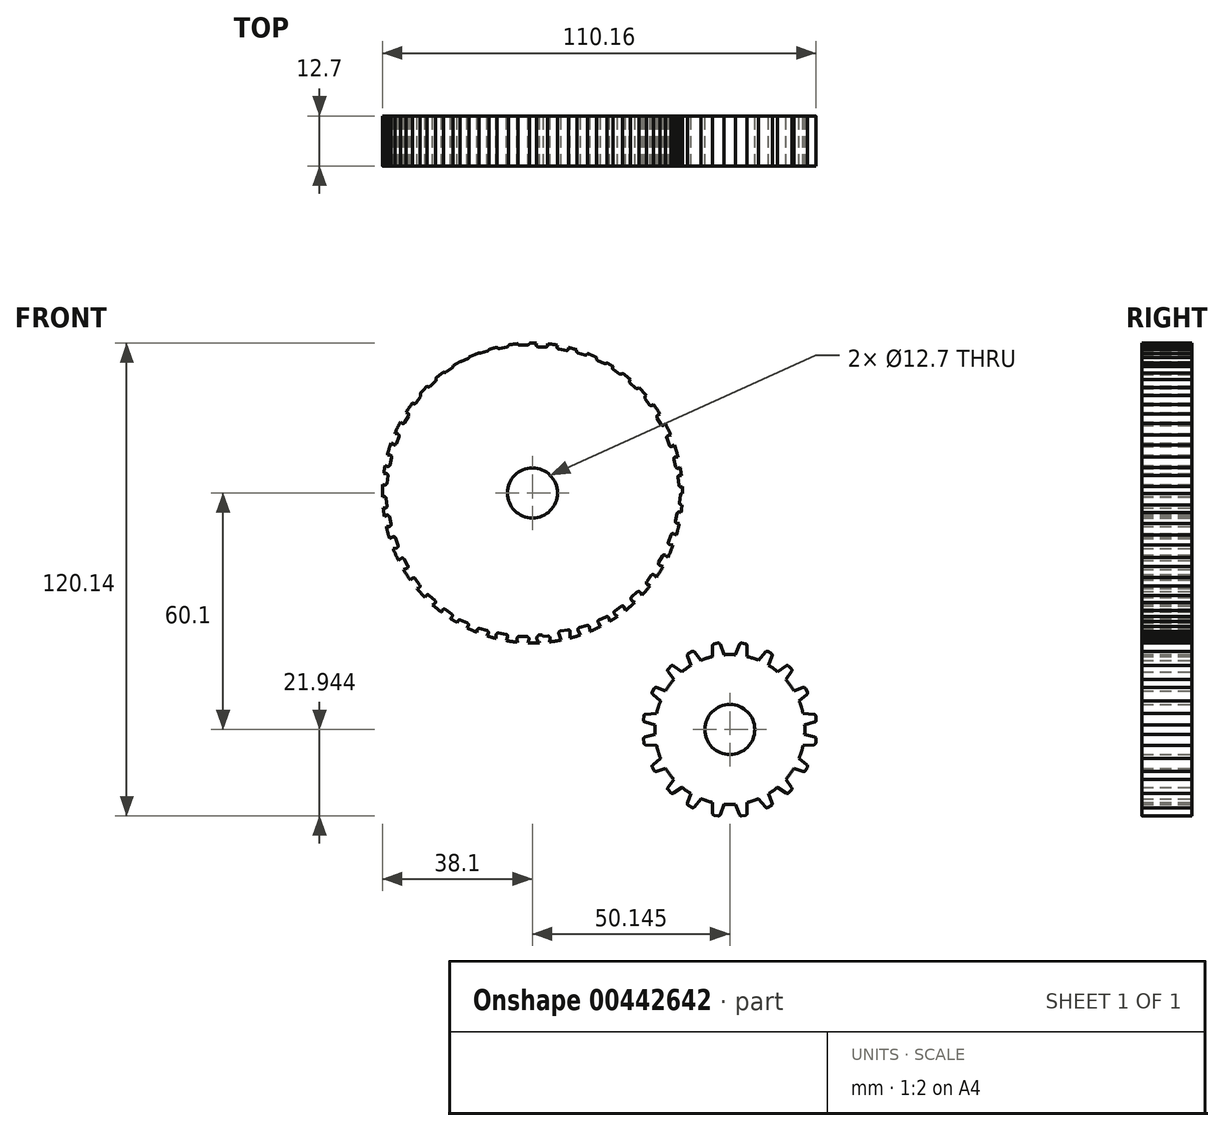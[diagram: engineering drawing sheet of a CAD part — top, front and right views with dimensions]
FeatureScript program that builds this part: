
annotation { "Feature Type Name" : "Feature", "Feature Type Description" : "" }
export const myFeature = defineFeature(function(context is Context, id is Id, definition is map)
    precondition{}
    {
        {
            var Q0;
            Q0=qCreatedBy(makeId("Front.planeOp"),FACE);
            var sketch = newSketch(context, id + "F0", { "sketchPlane" : qUnion([Q0])});
            skCircle(sketch, "E0", {"center": v(-27.1, 27.65) * mm, "radius": 38.1 * mm});
            skCircle(sketch, "E1", {"center": v(-27.1, 27.65) * mm, "radius": 6.35 * mm});
            skLineSegment(sketch, "E2", {"start": v(-65.2, 27.65) * mm, "end": v(11, 27.65) * mm, "construction": true});
            skLineSegment(sketch, "E3", {"start": v(-27.1, 65.75) * mm, "end": v(-27.1, -10.45) * mm, "construction": true});
            skLineSegment(sketch, "E4.MirrorCS", {"start": v(11, 27.65) * mm, "end": v(-65.2, 27.65) * mm, "construction": true});
            skLineSegment(sketch, "E5.MirrorCS", {"start": v(-30.36, 68.9) * mm, "end": v(-28.52, 68.98) * mm, "construction": true});
            skArc(sketch, "E6.MirrorCS", {"start": v(-41.25, 66.38) * mm, "mid": v(-41.16, 66.72) * mm, "end": v(-40.88, 66.92) * mm});
            skArc(sketch, "E7.MirrorCS", {"start": v(-28.95, 68.96) * mm, "mid": v(-28.62, 68.86) * mm, "end": v(-28.43, 68.56) * mm});
            skLineSegment(sketch, "E8.MirrorCS", {"start": v(-28.95, 68.96) * mm, "end": v(-29.93, 68.92) * mm});
            skLineSegment(sketch, "E9.MirrorCS", {"start": v(-39.93, 67.2) * mm, "end": v(-40.88, 66.92) * mm});
            skLineSegment(sketch, "E10.MirrorCS", {"start": v(-36.12, 68.01) * mm, "end": v(-34.3, 68.34) * mm, "construction": true});
            skLineSegment(sketch, "E11.MirrorCS", {"start": v(-55.6, 57.53) * mm, "end": v(-54.24, 58.77) * mm, "construction": true});
            skLineSegment(sketch, "E12.MirrorCS", {"start": v(-66.59, 37.04) * mm, "end": v(-66.8, 36.08) * mm});
            skLineSegment(sketch, "E13.MirrorCS", {"start": v(-64.7, 42.84) * mm, "end": v(-65.03, 41.91) * mm});
            skLineSegment(sketch, "E14.MirrorCS", {"start": v(-45.34, 65.04) * mm, "end": v(-46.25, 64.66) * mm});
            skArc(sketch, "E15.MirrorCS", {"start": v(-54.55, 58.48) * mm, "mid": v(-54.23, 58.61) * mm, "end": v(-53.9, 58.5) * mm});
            skArc(sketch, "E16.MirrorCS", {"start": v(-45.34, 65.04) * mm, "mid": v(-45, 65.06) * mm, "end": v(-44.72, 64.85) * mm});
            skArc(sketch, "E17.MirrorCS", {"start": v(-30.42, 68.48) * mm, "mid": v(-30.25, 68.79) * mm, "end": v(-29.93, 68.92) * mm});
            skLineSegment(sketch, "E18.MirrorCS", {"start": v(-54.55, 58.48) * mm, "end": v(-55.28, 57.82) * mm});
            skLineSegment(sketch, "E19.MirrorCS", {"start": v(-41.3, 66.8) * mm, "end": v(-39.52, 67.3) * mm, "construction": true});
            skArc(sketch, "E20.MirrorCS", {"start": v(-50.97, 61.04) * mm, "mid": v(-51, 61.4) * mm, "end": v(-50.8, 61.68) * mm});
            skArc(sketch, "E21.MirrorCS", {"start": v(-47.4, 60.28) * mm, "mid": v(-47.25, 59.87) * mm, "end": v(-47.46, 59.5) * mm});
            skArc(sketch, "E22.MirrorCS", {"start": v(-39.93, 67.2) * mm, "mid": v(-39.59, 67.17) * mm, "end": v(-39.34, 66.92) * mm});
            skLineSegment(sketch, "E23.MirrorCS", {"start": v(-49.35, 62.2) * mm, "end": v(-47.4, 60.28) * mm});
            skArc(sketch, "E24.MirrorCS", {"start": v(-50, 62.25) * mm, "mid": v(-49.67, 62.34) * mm, "end": v(-49.35, 62.2) * mm});
            skArc(sketch, "E25.MirrorCS", {"start": v(-55.76, 52.86) * mm, "mid": v(-55.48, 52.53) * mm, "end": v(-55.56, 52.1) * mm});
            skLineSegment(sketch, "E26.MirrorCS", {"start": v(-50, 62.25) * mm, "end": v(-50.8, 61.68) * mm});
            skLineSegment(sketch, "E27.MirrorCS", {"start": v(-66.9, 35.66) * mm, "end": v(-66.5, 37.45) * mm, "construction": true});
            skArc(sketch, "E28.MirrorCS", {"start": v(-66.5, 35.5) * mm, "mid": v(-66.76, 35.73) * mm, "end": v(-66.8, 36.08) * mm});
            skArc(sketch, "E29.MirrorCS", {"start": v(-36.12, 67.59) * mm, "mid": v(-36, 67.91) * mm, "end": v(-35.7, 68.09) * mm});
            skLineSegment(sketch, "E30.MirrorCS", {"start": v(-46.65, 64.5) * mm, "end": v(-44.95, 65.2) * mm, "construction": true});
            skArc(sketch, "E31.MirrorCS", {"start": v(-35.51, 64.35) * mm, "mid": v(-35.93, 64.46) * mm, "end": v(-36.1, 64.84) * mm});
            skArc(sketch, "E32.MirrorCS", {"start": v(-46.55, 64.08) * mm, "mid": v(-46.5, 64.42) * mm, "end": v(-46.25, 64.66) * mm});
            skArc(sketch, "E33.MirrorCS", {"start": v(-66.59, 37.04) * mm, "mid": v(-66.4, 37.33) * mm, "end": v(-66.07, 37.43) * mm});
            skArc(sketch, "E34.MirrorCS", {"start": v(-55.37, 57.17) * mm, "mid": v(-55.45, 57.5) * mm, "end": v(-55.28, 57.82) * mm});
            skArc(sketch, "E35.MirrorCS", {"start": v(-34.73, 68.26) * mm, "mid": v(-34.38, 68.2) * mm, "end": v(-34.16, 67.94) * mm});
            skLineSegment(sketch, "E36.MirrorCS", {"start": v(-34.73, 68.26) * mm, "end": v(-35.7, 68.09) * mm});
            skArc(sketch, "E37.MirrorCS", {"start": v(-61.43, 42.72) * mm, "mid": v(-61.08, 42.47) * mm, "end": v(-61.04, 42.05) * mm});
            skArc(sketch, "E38.MirrorCS", {"start": v(-64.7, 42.84) * mm, "mid": v(-64.48, 43.1) * mm, "end": v(-64.14, 43.17) * mm});
            skArc(sketch, "E39.MirrorCS", {"start": v(-67.36, 30.53) * mm, "mid": v(-67.64, 30.74) * mm, "end": v(-67.71, 31.08) * mm});
            skLineSegment(sketch, "E40.MirrorCS", {"start": v(-55.56, 52.1) * mm, "end": v(-56.68, 50.52) * mm});
            skArc(sketch, "E41.MirrorCS", {"start": v(-67.58, 32.05) * mm, "mid": v(-67.42, 32.36) * mm, "end": v(-67.1, 32.5) * mm});
            skLineSegment(sketch, "E42.MirrorCS", {"start": v(-62.75, 47.45) * mm, "end": v(-61.83, 49.04) * mm, "construction": true});
            skArc(sketch, "E43.MirrorCS", {"start": v(-43.23, 62.55) * mm, "mid": v(-43.17, 62.12) * mm, "end": v(-43.46, 61.8) * mm});
            skArc(sketch, "E44.MirrorCS", {"start": v(-59.55, 45.55) * mm, "mid": v(-59.9, 45.3) * mm, "end": v(-60.32, 45.41) * mm});
            skLineSegment(sketch, "E45.MirrorCS", {"start": v(-67.58, 32.05) * mm, "end": v(-67.71, 31.08) * mm});
            skArc(sketch, "E46.MirrorCS", {"start": v(-62.42, 47.17) * mm, "mid": v(-62.6, 47.48) * mm, "end": v(-62.53, 47.82) * mm});
            skLineSegment(sketch, "E47.MirrorCS", {"start": v(-33.6, 64.69) * mm, "end": v(-35.51, 64.35) * mm});
            skArc(sketch, "E48.MirrorCS", {"start": v(-58.85, 47.96) * mm, "mid": v(-58.55, 47.65) * mm, "end": v(-58.58, 47.23) * mm});
            skLineSegment(sketch, "E49.MirrorCS", {"start": v(-67.77, 30.65) * mm, "end": v(-67.53, 32.48) * mm, "construction": true});
            skArc(sketch, "E50.MirrorCS", {"start": v(-30.25, 65.19) * mm, "mid": v(-30.65, 65.35) * mm, "end": v(-30.78, 65.76) * mm});
            skArc(sketch, "E51.MirrorCS", {"start": v(-62.04, 48.67) * mm, "mid": v(-61.77, 48.9) * mm, "end": v(-61.43, 48.9) * mm});
            skLineSegment(sketch, "E52.MirrorCS", {"start": v(-44.72, 64.85) * mm, "end": v(-43.23, 62.55) * mm});
            skArc(sketch, "E53.MirrorCS", {"start": v(-27.84, 65.89) * mm, "mid": v(-27.93, 65.47) * mm, "end": v(-28.32, 65.27) * mm});
            skLineSegment(sketch, "E54.MirrorCS", {"start": v(-62.04, 48.67) * mm, "end": v(-62.53, 47.82) * mm});
            skLineSegment(sketch, "E55.MirrorCS", {"start": v(-53.9, 58.5) * mm, "end": v(-51.73, 56.83) * mm});
            skLineSegment(sketch, "E56.MirrorCS", {"start": v(-43.46, 61.8) * mm, "end": v(-45.25, 61.05) * mm});
            skArc(sketch, "E57.MirrorCS", {"start": v(-40.33, 63.22) * mm, "mid": v(-40.75, 63.29) * mm, "end": v(-40.97, 63.65) * mm});
            skLineSegment(sketch, "E58.MirrorCS", {"start": v(-60.32, 45.41) * mm, "end": v(-62.42, 47.17) * mm});
            skLineSegment(sketch, "E59.MirrorCS", {"start": v(-51.7, 56.05) * mm, "end": v(-53.13, 54.75) * mm});
            skArc(sketch, "E60.MirrorCS", {"start": v(-38.14, 64.46) * mm, "mid": v(-38.14, 64.03) * mm, "end": v(-38.46, 63.75) * mm});
            skLineSegment(sketch, "E61.MirrorCS", {"start": v(-59.68, 52.71) * mm, "end": v(-58.62, 54.21) * mm, "construction": true});
            skArc(sketch, "E62.MirrorCS", {"start": v(-49.04, 58.38) * mm, "mid": v(-49.46, 58.3) * mm, "end": v(-49.8, 58.57) * mm});
            skArc(sketch, "E63.MirrorCS", {"start": v(-61.69, 40.22) * mm, "mid": v(-61.99, 39.91) * mm, "end": v(-62.42, 39.95) * mm});
            skArc(sketch, "E64.MirrorCS", {"start": v(-59.38, 52.41) * mm, "mid": v(-59.53, 52.73) * mm, "end": v(-59.44, 53.06) * mm});
            skLineSegment(sketch, "E65.MirrorCS", {"start": v(-58.58, 47.23) * mm, "end": v(-59.55, 45.55) * mm});
            skArc(sketch, "E66.MirrorCS", {"start": v(-56.68, 50.52) * mm, "mid": v(-57.05, 50.31) * mm, "end": v(-57.46, 50.46) * mm});
            skLineSegment(sketch, "E67.MirrorCS", {"start": v(-65.17, 41.5) * mm, "end": v(-64.56, 43.24) * mm, "construction": true});
            skLineSegment(sketch, "E68.MirrorCS", {"start": v(-58.87, 53.87) * mm, "end": v(-59.44, 53.06) * mm});
            skLineSegment(sketch, "E69.MirrorCS", {"start": v(-28.32, 65.27) * mm, "end": v(-30.25, 65.19) * mm});
            skArc(sketch, "E70.MirrorCS", {"start": v(-64.36, 32.61) * mm, "mid": v(-63.96, 32.45) * mm, "end": v(-63.84, 32.04) * mm});
            skArc(sketch, "E71.MirrorCS", {"start": v(-58.87, 53.87) * mm, "mid": v(-58.58, 54.06) * mm, "end": v(-58.23, 54.03) * mm});
            skLineSegment(sketch, "E72.MirrorCS", {"start": v(-63.84, 32.04) * mm, "end": v(-64.1, 30.11) * mm});
            skLineSegment(sketch, "E73.MirrorCS", {"start": v(-61.04, 42.05) * mm, "end": v(-61.69, 40.22) * mm});
            skLineSegment(sketch, "E74.MirrorCS", {"start": v(-38.46, 63.75) * mm, "end": v(-40.33, 63.22) * mm});
            skArc(sketch, "E75.MirrorCS", {"start": v(-63.28, 34.8) * mm, "mid": v(-63.54, 34.46) * mm, "end": v(-63.97, 34.44) * mm});
            skArc(sketch, "E76.MirrorCS", {"start": v(-64.1, 30.11) * mm, "mid": v(-64.32, 29.75) * mm, "end": v(-64.75, 29.7) * mm});
            skLineSegment(sketch, "E77.MirrorCS", {"start": v(-47.46, 59.5) * mm, "end": v(-49.04, 58.38) * mm});
            skArc(sketch, "E78.MirrorCS", {"start": v(-63.33, 37.3) * mm, "mid": v(-62.95, 37.1) * mm, "end": v(-62.86, 36.69) * mm});
            skLineSegment(sketch, "E79.MirrorCS", {"start": v(-58.23, 54.03) * mm, "end": v(-55.76, 52.86) * mm});
            skArc(sketch, "E80.MirrorCS", {"start": v(-33.22, 65.36) * mm, "mid": v(-33.25, 64.93) * mm, "end": v(-33.6, 64.69) * mm});
            skArc(sketch, "E81.MirrorCS", {"start": v(-45.25, 61.05) * mm, "mid": v(-45.68, 61.06) * mm, "end": v(-45.94, 61.4) * mm});
            skArc(sketch, "E82.MirrorCS", {"start": v(-51.73, 56.83) * mm, "mid": v(-51.53, 56.45) * mm, "end": v(-51.7, 56.05) * mm});
            skArc(sketch, "E83.MirrorCS", {"start": v(-53.13, 54.75) * mm, "mid": v(-53.54, 54.62) * mm, "end": v(-53.9, 54.85) * mm});
            skArc(sketch, "E84.MirrorCS", {"start": v(-64.8, 41.3) * mm, "mid": v(-65.03, 41.56) * mm, "end": v(-65.03, 41.91) * mm});
            skLineSegment(sketch, "E85.MirrorCS", {"start": v(-62.86, 36.69) * mm, "end": v(-63.28, 34.8) * mm});
            skLineSegment(sketch, "E86.MirrorCS", {"start": v(-62.42, 39.95) * mm, "end": v(-64.8, 41.3) * mm});
            skLineSegment(sketch, "E87.MirrorCS", {"start": v(-64.14, 43.17) * mm, "end": v(-61.43, 42.72) * mm});
            skLineSegment(sketch, "E88.MirrorCS", {"start": v(-63.97, 34.44) * mm, "end": v(-66.5, 35.5) * mm});
            skLineSegment(sketch, "E89.MirrorCS", {"start": v(-66.07, 37.43) * mm, "end": v(-63.33, 37.3) * mm});
            skLineSegment(sketch, "E90.MirrorCS", {"start": v(-34.16, 67.94) * mm, "end": v(-33.22, 65.36) * mm});
            skLineSegment(sketch, "E91.MirrorCS", {"start": v(-36.1, 64.84) * mm, "end": v(-36.12, 67.59) * mm});
            skLineSegment(sketch, "E92.MirrorCS", {"start": v(-45.94, 61.4) * mm, "end": v(-46.55, 64.08) * mm});
            skLineSegment(sketch, "E93.MirrorCS", {"start": v(-53.9, 54.85) * mm, "end": v(-55.37, 57.17) * mm});
            skPoint(sketch, "E94.MirrorP", {"position": v(-63.41, 34.2) * mm});
            skLineSegment(sketch, "E95.MirrorCS", {"start": v(-61.43, 48.9) * mm, "end": v(-58.85, 47.96) * mm});
            skLineSegment(sketch, "E96.MirrorCS", {"start": v(-30.78, 65.76) * mm, "end": v(-30.42, 68.48) * mm});
            skLineSegment(sketch, "E97.MirrorCS", {"start": v(-28.43, 68.56) * mm, "end": v(-27.84, 65.89) * mm});
            skLineSegment(sketch, "E98.MirrorCS", {"start": v(-40.97, 63.65) * mm, "end": v(-41.25, 66.38) * mm});
            skLineSegment(sketch, "E99.MirrorCS", {"start": v(-49.8, 58.57) * mm, "end": v(-50.97, 61.04) * mm});
            skLineSegment(sketch, "E100.MirrorCS", {"start": v(-39.34, 66.92) * mm, "end": v(-38.14, 64.46) * mm});
            skLineSegment(sketch, "E101.MirrorCS", {"start": v(-57.46, 50.46) * mm, "end": v(-59.38, 52.41) * mm});
            skPoint(sketch, "E102.MirrorP", {"position": v(-61.83, 49.04) * mm});
            skPoint(sketch, "E103.MirrorP", {"position": v(-64.56, 43.24) * mm});
            skPoint(sketch, "E104.MirrorP", {"position": v(-54.24, 58.77) * mm});
            skPoint(sketch, "E105.MirrorP", {"position": v(-35.83, 64.17) * mm});
            skPoint(sketch, "E106.MirrorP", {"position": v(-41.3, 66.8) * mm});
            skPoint(sketch, "E107.MirrorP", {"position": v(-30.36, 68.9) * mm});
            skPoint(sketch, "E108.MirrorP", {"position": v(-66.9, 35.66) * mm});
            skPoint(sketch, "E109.MirrorP", {"position": v(-59.68, 52.71) * mm});
            skPoint(sketch, "E110.MirrorP", {"position": v(-49.53, 58.02) * mm});
            skPoint(sketch, "E111.MirrorP", {"position": v(-40.9, 63.05) * mm});
            skPoint(sketch, "E112.MirrorP", {"position": v(-30.86, 65.16) * mm});
            skPoint(sketch, "E113.MirrorP", {"position": v(-57.03, 50.03) * mm});
            skPoint(sketch, "E114.MirrorP", {"position": v(-36.1, 64.24) * mm});
            skPoint(sketch, "E115.MirrorP", {"position": v(-27.9, 63.9) * mm});
            skPoint(sketch, "E116.MirrorP", {"position": v(-62.72, 37.28) * mm});
            skPoint(sketch, "E117.MirrorP", {"position": v(-55.2, 52.6) * mm});
            skPoint(sketch, "E118.MirrorP", {"position": v(-46.97, 59.85) * mm});
            skPoint(sketch, "E119.MirrorP", {"position": v(-37.88, 63.91) * mm});
            skLineSegment(sketch, "E120.MirrorCS", {"start": v(-64.75, 29.7) * mm, "end": v(-67.36, 30.53) * mm});
            skLineSegment(sketch, "E121.MirrorCS", {"start": v(-67.1, 32.5) * mm, "end": v(-64.36, 32.61) * mm});
            skPoint(sketch, "E122.MirrorP", {"position": v(-28.52, 68.98) * mm});
            skPoint(sketch, "E123.MirrorP", {"position": v(-66.5, 37.45) * mm});
            skPoint(sketch, "E124.MirrorP", {"position": v(-58.62, 54.21) * mm});
            skPoint(sketch, "E125.MirrorP", {"position": v(-39.52, 67.3) * mm});
            skPoint(sketch, "E126.MirrorP", {"position": v(-49.66, 62.5) * mm});
            skPoint(sketch, "E127.MirrorP", {"position": v(-67.77, 30.65) * mm});
            skPoint(sketch, "E128.MirrorP", {"position": v(-51.15, 61.43) * mm});
            skPoint(sketch, "E129.MirrorP", {"position": v(-36.12, 68.01) * mm});
            skPoint(sketch, "E130.MirrorP", {"position": v(-65.17, 41.5) * mm});
            skPoint(sketch, "E131.MirrorP", {"position": v(-67.53, 32.48) * mm});
            skPoint(sketch, "E132.MirrorP", {"position": v(-62.75, 47.45) * mm});
            skPoint(sketch, "E133.MirrorP", {"position": v(-55.6, 57.53) * mm});
            skPoint(sketch, "E134.MirrorP", {"position": v(-42.12, 66.67) * mm});
            skPoint(sketch, "E135.MirrorP", {"position": v(-64.17, 29.23) * mm});
            skPoint(sketch, "E136.MirrorP", {"position": v(-61.9, 39.65) * mm});
            skPoint(sketch, "E137.MirrorP", {"position": v(-63.46, 33.39) * mm});
            skPoint(sketch, "E138.MirrorP", {"position": v(-53.58, 54.34) * mm});
            skPoint(sketch, "E139.MirrorP", {"position": v(-59.86, 45.02) * mm});
            skPoint(sketch, "E140.MirrorP", {"position": v(-41.6, 62.93) * mm});
            skPoint(sketch, "E141.MirrorP", {"position": v(-44.95, 65.2) * mm});
            skPoint(sketch, "E142.MirrorP", {"position": v(-34.3, 68.34) * mm});
            skPoint(sketch, "E143.MirrorP", {"position": v(-60.84, 42.62) * mm});
            skPoint(sketch, "E144.MirrorP", {"position": v(-58.28, 47.75) * mm});
            skPoint(sketch, "E145.MirrorP", {"position": v(-51.25, 56.46) * mm});
            skPoint(sketch, "E146.MirrorP", {"position": v(-42.9, 62.04) * mm});
            skArc(sketch, "E147.MirrorCS", {"start": v(-13.68, -9.96) * mm, "mid": v(-14.02, -9.93) * mm, "end": v(-14.27, -9.7) * mm});
            skArc(sketch, "E148.MirrorCS", {"start": v(5.77, 4.82) * mm, "mid": v(5.92, 4.5) * mm, "end": v(5.83, 4.17) * mm});
            skArc(sketch, "E149.MirrorCS", {"start": v(7.83, 14.52) * mm, "mid": v(7.47, 14.76) * mm, "end": v(7.43, 15.19) * mm});
            skLineSegment(sketch, "E150.MirrorCS", {"start": v(12.98, 20.2) * mm, "end": v(13.2, 21.16) * mm});
            skLineSegment(sketch, "E151.MirrorCS", {"start": v(-18.88, -11.03) * mm, "end": v(-17.91, -10.86) * mm});
            skArc(sketch, "E152.MirrorCS", {"start": v(-10.38, -5.31) * mm, "mid": v(-10.44, -4.89) * mm, "end": v(-10.15, -4.57) * mm});
            skLineSegment(sketch, "E153.MirrorCS", {"start": v(9.14, 9.78) * mm, "end": v(8.22, 8.2) * mm, "construction": true});
            skLineSegment(sketch, "E154.MirrorCS", {"start": v(-62.93, 8.97) * mm, "end": v(-62.01, 7.38) * mm, "construction": true});
            skLineSegment(sketch, "E155.MirrorCS", {"start": v(-23.07, -12.4) * mm, "end": v(-24.9, -12.48) * mm, "construction": true});
            skArc(sketch, "E156.MirrorCS", {"start": v(0.95, -1.25) * mm, "mid": v(0.62, -1.38) * mm, "end": v(0.3, -1.27) * mm});
            skLineSegment(sketch, "E157.MirrorCS", {"start": v(-8.26, -7.8) * mm, "end": v(-7.36, -7.43) * mm});
            skArc(sketch, "E158.MirrorCS", {"start": v(-18.88, -11.03) * mm, "mid": v(-19.23, -10.97) * mm, "end": v(-19.45, -10.7) * mm});
            skArc(sketch, "E159.MirrorCS", {"start": v(1.76, 0.06) * mm, "mid": v(1.84, -0.28) * mm, "end": v(1.67, -0.58) * mm});
            skArc(sketch, "E160.MirrorCS", {"start": v(-23.03, -12.14) * mm, "mid": v(-23.28, -12.4) * mm, "end": v(-23.64, -12.43) * mm});
            skLineSegment(sketch, "E161.MirrorCS", {"start": v(-46.83, -8.07) * mm, "end": v(-45.14, -8.79) * mm, "construction": true});
            skLineSegment(sketch, "E162.MirrorCS", {"start": v(-45.53, -8.62) * mm, "end": v(-46.44, -8.24) * mm});
            skLineSegment(sketch, "E163.MirrorCS", {"start": v(14.16, 26.58) * mm, "end": v(13.92, 24.75) * mm, "construction": true});
            skArc(sketch, "E164.MirrorCS", {"start": v(5.24, 9.28) * mm, "mid": v(4.94, 9.58) * mm, "end": v(4.97, 10) * mm});
            skLineSegment(sketch, "E165.MirrorCS", {"start": v(0.95, -1.25) * mm, "end": v(1.67, -0.58) * mm});
            skArc(sketch, "E166.MirrorCS", {"start": v(12.98, 20.2) * mm, "mid": v(12.79, 19.9) * mm, "end": v(12.46, 19.8) * mm});
            skArc(sketch, "E167.MirrorCS", {"start": v(-20.4, -8.13) * mm, "mid": v(-20.36, -7.7) * mm, "end": v(-20, -7.45) * mm});
            skArc(sketch, "E168.MirrorCS", {"start": v(-7.06, -6.84) * mm, "mid": v(-7.1, -7.19) * mm, "end": v(-7.36, -7.43) * mm});
            skLineSegment(sketch, "E169.MirrorCS", {"start": v(-12.32, -9.57) * mm, "end": v(-14.09, -10.08) * mm, "construction": true});
            skArc(sketch, "E170.MirrorCS", {"start": v(-23.17, -8.7) * mm, "mid": v(-22.78, -8.86) * mm, "end": v(-22.65, -9.27) * mm});
            skLineSegment(sketch, "E171.MirrorCS", {"start": v(1.99, -0.3) * mm, "end": v(0.63, -1.54) * mm, "construction": true});
            skLineSegment(sketch, "E172.MirrorCS", {"start": v(-29.13, -12.54) * mm, "end": v(-30.12, -12.5) * mm});
            skArc(sketch, "E173.MirrorCS", {"start": v(8.43, 8.56) * mm, "mid": v(8.16, 8.34) * mm, "end": v(7.82, 8.34) * mm});
            skArc(sketch, "E174.MirrorCS", {"start": v(9.72, 19.93) * mm, "mid": v(9.34, 20.13) * mm, "end": v(9.25, 20.54) * mm});
            skLineSegment(sketch, "E175.MirrorCS", {"start": v(-6.96, -7.26) * mm, "end": v(-8.66, -7.97) * mm, "construction": true});
            skLineSegment(sketch, "E176.MirrorCS", {"start": v(-6.15, -2.27) * mm, "end": v(-4.57, -1.14) * mm});
            skArc(sketch, "E177.MirrorCS", {"start": v(-12.36, -9.15) * mm, "mid": v(-12.44, -9.49) * mm, "end": v(-12.73, -9.69) * mm});
            skArc(sketch, "E178.MirrorCS", {"start": v(-29.13, -12.54) * mm, "mid": v(-28.8, -12.44) * mm, "end": v(-28.62, -12.14) * mm});
            skLineSegment(sketch, "E179.MirrorCS", {"start": v(8.43, 8.56) * mm, "end": v(8.92, 9.41) * mm});
            skArc(sketch, "E180.MirrorCS", {"start": v(-17.5, -10.35) * mm, "mid": v(-17.61, -10.68) * mm, "end": v(-17.91, -10.86) * mm});
            skLineSegment(sketch, "E181.MirrorCS", {"start": v(5.26, 3.37) * mm, "end": v(5.83, 4.17) * mm});
            skArc(sketch, "E182.MirrorCS", {"start": v(-46.74, -7.66) * mm, "mid": v(-46.7, -8) * mm, "end": v(-46.44, -8.24) * mm});
            skArc(sketch, "E183.MirrorCS", {"start": v(-13.28, -5.98) * mm, "mid": v(-12.86, -6.05) * mm, "end": v(-12.64, -6.42) * mm});
            skArc(sketch, "E184.MirrorCS", {"start": v(-24.63, -12.47) * mm, "mid": v(-24.82, -12.38) * mm, "end": v(-24.96, -12.22) * mm});
            skArc(sketch, "E185.MirrorCS", {"start": v(12.9, 21.74) * mm, "mid": v(13.15, 21.5) * mm, "end": v(13.2, 21.16) * mm});
            skLineSegment(sketch, "E186.MirrorCS", {"start": v(-17.5, -10.78) * mm, "end": v(-19.3, -11.1) * mm, "construction": true});
            skArc(sketch, "E187.MirrorCS", {"start": v(-2.64, -3.81) * mm, "mid": v(-2.6, -4.16) * mm, "end": v(-2.8, -4.44) * mm});
            skArc(sketch, "E188.MirrorCS", {"start": v(5.26, 3.37) * mm, "mid": v(4.97, 3.17) * mm, "end": v(4.63, 3.2) * mm});
            skLineSegment(sketch, "E189.MirrorCS", {"start": v(11.56, 15.72) * mm, "end": v(10.95, 14) * mm, "construction": true});
            skArc(sketch, "E190.MirrorCS", {"start": v(-30.6, -12.06) * mm, "mid": v(-30.44, -12.37) * mm, "end": v(-30.12, -12.5) * mm});
            skArc(sketch, "E191.MirrorCS", {"start": v(-53.32, 1.67) * mm, "mid": v(-53.73, 1.8) * mm, "end": v(-54.1, 1.57) * mm});
            skLineSegment(sketch, "E192.MirrorCS", {"start": v(13.29, 21.57) * mm, "end": v(12.88, 19.78) * mm, "construction": true});
            skLineSegment(sketch, "E193.MirrorCS", {"start": v(-24.63, -12.47) * mm, "end": v(-23.64, -12.43) * mm});
            skLineSegment(sketch, "E194.MirrorCS", {"start": v(-30.55, -12.48) * mm, "end": v(-28.7, -12.56) * mm, "construction": true});
            skLineSegment(sketch, "E195.MirrorCS", {"start": v(6.07, 4.52) * mm, "end": v(5.01, 3.02) * mm, "construction": true});
            skArc(sketch, "E196.MirrorCS", {"start": v(-4.57, -1.14) * mm, "mid": v(-4.15, -1.06) * mm, "end": v(-3.82, -1.34) * mm});
            skLineSegment(sketch, "E197.MirrorCS", {"start": v(-3.6, -5.02) * mm, "end": v(-2.8, -4.44) * mm});
            skArc(sketch, "E198.MirrorCS", {"start": v(2.15, 4.37) * mm, "mid": v(1.87, 4.7) * mm, "end": v(1.95, 5.13) * mm});
            skLineSegment(sketch, "E199.MirrorCS", {"start": v(-13.68, -9.96) * mm, "end": v(-12.73, -9.69) * mm});
            skArc(sketch, "E200.MirrorCS", {"start": v(-6.21, -3.04) * mm, "mid": v(-6.36, -2.64) * mm, "end": v(-6.15, -2.27) * mm});
            skArc(sketch, "E201.MirrorCS", {"start": v(-8.26, -7.8) * mm, "mid": v(-8.61, -7.83) * mm, "end": v(-8.89, -7.62) * mm});
            skArc(sketch, "E202.MirrorCS", {"start": v(8.81, 10.06) * mm, "mid": v(8.98, 9.76) * mm, "end": v(8.92, 9.41) * mm});
            skArc(sketch, "E203.MirrorCS", {"start": v(11.1, 14.4) * mm, "mid": v(10.87, 14.12) * mm, "end": v(10.53, 14.06) * mm});
            skLineSegment(sketch, "E204.MirrorCS", {"start": v(11.1, 14.4) * mm, "end": v(11.42, 15.32) * mm});
            skLineSegment(sketch, "E205.MirrorCS", {"start": v(7.43, 15.19) * mm, "end": v(8.08, 17.01) * mm});
            skLineSegment(sketch, "E206.MirrorCS", {"start": v(9.25, 20.54) * mm, "end": v(9.67, 22.44) * mm});
            skArc(sketch, "E207.MirrorCS", {"start": v(11.2, 15.93) * mm, "mid": v(11.42, 15.67) * mm, "end": v(11.42, 15.32) * mm});
            skArc(sketch, "E208.MirrorCS", {"start": v(-59.74, 10.87) * mm, "mid": v(-60.1, 11.12) * mm, "end": v(-60.5, 11) * mm});
            skArc(sketch, "E209.MirrorCS", {"start": v(8.08, 17.01) * mm, "mid": v(8.38, 17.32) * mm, "end": v(8.8, 17.29) * mm});
            skLineSegment(sketch, "E210.MirrorCS", {"start": v(-34.91, -11.84) * mm, "end": v(-35.88, -11.67) * mm});
            skLineSegment(sketch, "E211.MirrorCS", {"start": v(13.97, 25.18) * mm, "end": v(14.1, 26.16) * mm});
            skLineSegment(sketch, "E212.MirrorCS", {"start": v(-54.74, -2.06) * mm, "end": v(-55.47, -1.4) * mm});
            skLineSegment(sketch, "E213.MirrorCS", {"start": v(4.97, 10) * mm, "end": v(5.94, 11.69) * mm});
            skLineSegment(sketch, "E214.MirrorCS", {"start": v(10.36, 22.8) * mm, "end": v(12.9, 21.74) * mm});
            skArc(sketch, "E215.MirrorCS", {"start": v(-56.87, 5.9) * mm, "mid": v(-57.24, 6.1) * mm, "end": v(-57.64, 5.96) * mm});
            skArc(sketch, "E216.MirrorCS", {"start": v(-0.48, 2.48) * mm, "mid": v(-0.07, 2.61) * mm, "end": v(0.3, 2.38) * mm});
            skArc(sketch, "E217.MirrorCS", {"start": v(-66.69, 20.92) * mm, "mid": v(-66.95, 20.69) * mm, "end": v(-66.99, 20.34) * mm});
            skLineSegment(sketch, "E218.MirrorCS", {"start": v(-66.77, 19.38) * mm, "end": v(-66.99, 20.34) * mm});
            skArc(sketch, "E219.MirrorCS", {"start": v(13.97, 25.18) * mm, "mid": v(13.81, 24.87) * mm, "end": v(13.5, 24.74) * mm});
            skArc(sketch, "E220.MirrorCS", {"start": v(-38.33, -8.04) * mm, "mid": v(-38.32, -7.6) * mm, "end": v(-38.65, -7.33) * mm});
            skLineSegment(sketch, "E221.MirrorCS", {"start": v(-38.65, -7.33) * mm, "end": v(-40.51, -6.8) * mm});
            skLineSegment(sketch, "E222.MirrorCS", {"start": v(-60.5, 11) * mm, "end": v(-62.6, 9.24) * mm});
            skLineSegment(sketch, "E223.MirrorCS", {"start": v(-36.3, -11.6) * mm, "end": v(-34.5, -11.92) * mm, "construction": true});
            skArc(sketch, "E224.MirrorCS", {"start": v(5.94, 11.69) * mm, "mid": v(6.3, 11.93) * mm, "end": v(6.71, 11.82) * mm});
            skLineSegment(sketch, "E225.MirrorCS", {"start": v(-50.2, -5.83) * mm, "end": v(-51, -5.26) * mm});
            skArc(sketch, "E226.MirrorCS", {"start": v(-8.36, -3.82) * mm, "mid": v(-7.93, -3.83) * mm, "end": v(-7.67, -4.17) * mm});
            skLineSegment(sketch, "E227.MirrorCS", {"start": v(1.95, 5.13) * mm, "end": v(3.07, 6.7) * mm});
            skLineSegment(sketch, "E228.MirrorCS", {"start": v(-67.77, 24.36) * mm, "end": v(-67.9, 25.34) * mm});
            skArc(sketch, "E229.MirrorCS", {"start": v(-36.3, -11.17) * mm, "mid": v(-36.18, -11.5) * mm, "end": v(-35.88, -11.67) * mm});
            skArc(sketch, "E230.MirrorCS", {"start": v(-67.77, 24.36) * mm, "mid": v(-67.6, 24.06) * mm, "end": v(-67.29, 23.92) * mm});
            skArc(sketch, "E231.MirrorCS", {"start": v(-40.51, -6.8) * mm, "mid": v(-40.94, -6.87) * mm, "end": v(-41.16, -7.23) * mm});
            skLineSegment(sketch, "E232.MirrorCS", {"start": v(-20, -7.45) * mm, "end": v(-18.1, -7.11) * mm});
            skLineSegment(sketch, "E233.MirrorCS", {"start": v(-61.23, 14.37) * mm, "end": v(-61.88, 16.2) * mm});
            skLineSegment(sketch, "E234.MirrorCS", {"start": v(-64.89, 13.58) * mm, "end": v(-65.22, 14.5) * mm});
            skArc(sketch, "E235.MirrorCS", {"start": v(13.75, 26.7) * mm, "mid": v(14.03, 26.5) * mm, "end": v(14.1, 26.16) * mm});
            skLineSegment(sketch, "E236.MirrorCS", {"start": v(-54.1, 1.57) * mm, "end": v(-55.56, -0.75) * mm});
            skLineSegment(sketch, "E237.MirrorCS", {"start": v(-47.64, -3.08) * mm, "end": v(-49.22, -1.96) * mm});
            skLineSegment(sketch, "E238.MirrorCS", {"start": v(-59.87, 3.7) * mm, "end": v(-58.8, 2.2) * mm, "construction": true});
            skLineSegment(sketch, "E239.MirrorCS", {"start": v(-40.12, -10.77) * mm, "end": v(-41.07, -10.5) * mm});
            skArc(sketch, "E240.MirrorCS", {"start": v(-62.6, 9.24) * mm, "mid": v(-62.78, 8.94) * mm, "end": v(-62.72, 8.6) * mm});
            skArc(sketch, "E241.MirrorCS", {"start": v(-55.94, 3.56) * mm, "mid": v(-55.67, 3.9) * mm, "end": v(-55.75, 4.31) * mm});
            skArc(sketch, "E242.MirrorCS", {"start": v(-63.52, 19.11) * mm, "mid": v(-63.13, 19.31) * mm, "end": v(-63.04, 19.73) * mm});
            skArc(sketch, "E243.MirrorCS", {"start": v(-49.22, -1.96) * mm, "mid": v(-49.65, -1.88) * mm, "end": v(-49.98, -2.15) * mm});
            skLineSegment(sketch, "E244.MirrorCS", {"start": v(-55.75, 4.31) * mm, "end": v(-56.87, 5.9) * mm});
            skLineSegment(sketch, "E245.MirrorCS", {"start": v(-43.65, -5.38) * mm, "end": v(-45.44, -4.63) * mm});
            skLineSegment(sketch, "E246.MirrorCS", {"start": v(-64.02, 24.38) * mm, "end": v(-64.28, 26.3) * mm});
            skArc(sketch, "E247.MirrorCS", {"start": v(-50.2, -5.83) * mm, "mid": v(-49.86, -5.92) * mm, "end": v(-49.54, -5.78) * mm});
            skLineSegment(sketch, "E248.MirrorCS", {"start": v(-58.42, 2.39) * mm, "end": v(-55.94, 3.56) * mm});
            skArc(sketch, "E249.MirrorCS", {"start": v(-61.88, 16.2) * mm, "mid": v(-62.18, 16.5) * mm, "end": v(-62.6, 16.47) * mm});
            skLineSegment(sketch, "E250.MirrorCS", {"start": v(0.3, 2.38) * mm, "end": v(1.76, 0.06) * mm});
            skArc(sketch, "E251.MirrorCS", {"start": v(-33.4, -8.94) * mm, "mid": v(-33.44, -8.51) * mm, "end": v(-33.79, -8.27) * mm});
            skLineSegment(sketch, "E252.MirrorCS", {"start": v(-8.89, -7.62) * mm, "end": v(-10.38, -5.31) * mm});
            skArc(sketch, "E253.MirrorCS", {"start": v(-18.1, -7.11) * mm, "mid": v(-17.68, -7.22) * mm, "end": v(-17.5, -7.61) * mm});
            skLineSegment(sketch, "E254.MirrorCS", {"start": v(3.85, 6.77) * mm, "end": v(5.77, 4.82) * mm});
            skLineSegment(sketch, "E255.MirrorCS", {"start": v(-33.79, -8.27) * mm, "end": v(-35.7, -7.93) * mm});
            skArc(sketch, "E256.MirrorCS", {"start": v(-35.7, -7.93) * mm, "mid": v(-36.11, -8.04) * mm, "end": v(-36.3, -8.42) * mm});
            skArc(sketch, "E257.MirrorCS", {"start": v(-54.74, -2.06) * mm, "mid": v(-54.42, -2.2) * mm, "end": v(-54.09, -2.09) * mm});
            skArc(sketch, "E258.MirrorCS", {"start": v(-67.55, 25.9) * mm, "mid": v(-67.82, 25.68) * mm, "end": v(-67.9, 25.34) * mm});
            skLineSegment(sketch, "E259.MirrorCS", {"start": v(-54.09, -2.09) * mm, "end": v(-51.92, -0.41) * mm});
            skArc(sketch, "E260.MirrorCS", {"start": v(-59.05, 2.55) * mm, "mid": v(-58.77, 2.36) * mm, "end": v(-58.42, 2.39) * mm});
            skArc(sketch, "E261.MirrorCS", {"start": v(-25.75, -8.65) * mm, "mid": v(-24.36, -9.84) * mm, "end": v(-25.87, -8.8) * mm});
            skLineSegment(sketch, "E262.MirrorCS", {"start": v(-49.54, -5.78) * mm, "end": v(-47.58, -3.86) * mm});
            skArc(sketch, "E263.MirrorCS", {"start": v(10.48, 27.12) * mm, "mid": v(10.71, 27.48) * mm, "end": v(11.14, 27.53) * mm});
            skLineSegment(sketch, "E264.MirrorCS", {"start": v(0.3, -1.27) * mm, "end": v(-1.88, 0.4) * mm});
            skLineSegment(sketch, "E265.MirrorCS", {"start": v(-10.15, -4.57) * mm, "end": v(-8.36, -3.82) * mm});
            skLineSegment(sketch, "E266.MirrorCS", {"start": v(10.23, 25.2) * mm, "end": v(10.48, 27.12) * mm});
            skArc(sketch, "E267.MirrorCS", {"start": v(9.67, 22.44) * mm, "mid": v(9.93, 22.78) * mm, "end": v(10.36, 22.8) * mm});
            skLineSegment(sketch, "E268.MirrorCS", {"start": v(-15.15, -6.51) * mm, "end": v(-13.28, -5.98) * mm});
            skLineSegment(sketch, "E269.MirrorCS", {"start": v(-4.26, -4.97) * mm, "end": v(-6.21, -3.04) * mm});
            skArc(sketch, "E270.MirrorCS", {"start": v(-59.04, 8.46) * mm, "mid": v(-58.73, 8.77) * mm, "end": v(-58.77, 9.2) * mm});
            skArc(sketch, "E271.MirrorCS", {"start": v(-64.28, 26.3) * mm, "mid": v(-64.5, 26.67) * mm, "end": v(-64.94, 26.72) * mm});
            skArc(sketch, "E272.MirrorCS", {"start": v(-45.53, -8.62) * mm, "mid": v(-45.18, -8.64) * mm, "end": v(-44.9, -8.43) * mm});
            skArc(sketch, "E273.MirrorCS", {"start": v(-59.57, 4) * mm, "mid": v(-59.71, 3.7) * mm, "end": v(-59.62, 3.36) * mm});
            skArc(sketch, "E274.MirrorCS", {"start": v(-64.89, 13.58) * mm, "mid": v(-64.67, 13.31) * mm, "end": v(-64.32, 13.25) * mm});
            skLineSegment(sketch, "E275.MirrorCS", {"start": v(-62.23, 7.75) * mm, "end": v(-62.72, 8.6) * mm});
            skArc(sketch, "E276.MirrorCS", {"start": v(-64.55, 23.8) * mm, "mid": v(-64.15, 23.97) * mm, "end": v(-64.02, 24.38) * mm});
            skLineSegment(sketch, "E277.MirrorCS", {"start": v(-62.6, 16.47) * mm, "end": v(-64.99, 15.12) * mm});
            skLineSegment(sketch, "E278.MirrorCS", {"start": v(-65.36, 14.91) * mm, "end": v(-64.75, 13.18) * mm, "construction": true});
            skArc(sketch, "E279.MirrorCS", {"start": v(-51.16, -4.63) * mm, "mid": v(-51.2, -4.97) * mm, "end": v(-51, -5.26) * mm});
            skArc(sketch, "E280.MirrorCS", {"start": v(-41.44, -9.96) * mm, "mid": v(-41.35, -10.3) * mm, "end": v(-41.07, -10.5) * mm});
            skArc(sketch, "E281.MirrorCS", {"start": v(-40.12, -10.77) * mm, "mid": v(-39.77, -10.75) * mm, "end": v(-39.52, -10.5) * mm});
            skLineSegment(sketch, "E282.MirrorCS", {"start": v(6.71, 11.82) * mm, "end": v(8.81, 10.06) * mm});
            skLineSegment(sketch, "E283.MirrorCS", {"start": v(-1.9, 1.18) * mm, "end": v(-0.48, 2.48) * mm});
            skLineSegment(sketch, "E284.MirrorCS", {"start": v(-67.96, 25.76) * mm, "end": v(-67.71, 23.94) * mm, "construction": true});
            skArc(sketch, "E285.MirrorCS", {"start": v(-66.77, 19.38) * mm, "mid": v(-66.59, 19.09) * mm, "end": v(-66.25, 18.99) * mm});
            skArc(sketch, "E286.MirrorCS", {"start": v(10.75, 24.62) * mm, "mid": v(10.35, 24.79) * mm, "end": v(10.23, 25.2) * mm});
            skArc(sketch, "E287.MirrorCS", {"start": v(-45.44, -4.63) * mm, "mid": v(-45.86, -4.65) * mm, "end": v(-46.13, -4.98) * mm});
            skLineSegment(sketch, "E288.MirrorCS", {"start": v(-58.77, 9.2) * mm, "end": v(-59.74, 10.87) * mm});
            skArc(sketch, "E289.MirrorCS", {"start": v(-61.62, 13.7) * mm, "mid": v(-61.27, 13.95) * mm, "end": v(-61.23, 14.37) * mm});
            skArc(sketch, "E290.MirrorCS", {"start": v(-28.03, -9.47) * mm, "mid": v(-28.12, -9.05) * mm, "end": v(-28.5, -8.85) * mm});
            skLineSegment(sketch, "E291.MirrorCS", {"start": v(-28.5, -8.85) * mm, "end": v(-30.44, -8.77) * mm});
            skLineSegment(sketch, "E292.MirrorCS", {"start": v(-63.04, 19.73) * mm, "end": v(-63.47, 21.62) * mm});
            skLineSegment(sketch, "E293.MirrorCS", {"start": v(-25.87, -8.8) * mm, "end": v(-23.17, -8.7) * mm});
            skArc(sketch, "E294.MirrorCS", {"start": v(-15.47, -7.22) * mm, "mid": v(-15.47, -6.8) * mm, "end": v(-15.15, -6.51) * mm});
            skArc(sketch, "E295.MirrorCS", {"start": v(-47.58, -3.86) * mm, "mid": v(-47.43, -3.45) * mm, "end": v(-47.64, -3.08) * mm});
            skLineSegment(sketch, "E296.MirrorCS", {"start": v(-44.9, -8.43) * mm, "end": v(-43.42, -6.13) * mm});
            skArc(sketch, "E297.MirrorCS", {"start": v(-30.44, -8.77) * mm, "mid": v(-30.83, -8.93) * mm, "end": v(-30.96, -9.34) * mm});
            skArc(sketch, "E298.MirrorCS", {"start": v(-55.56, -0.75) * mm, "mid": v(-55.63, -1.09) * mm, "end": v(-55.47, -1.4) * mm});
            skArc(sketch, "E299.MirrorCS", {"start": v(-63.47, 21.62) * mm, "mid": v(-63.73, 21.96) * mm, "end": v(-64.16, 21.98) * mm});
            skLineSegment(sketch, "E300.MirrorCS", {"start": v(-51.89, 0.37) * mm, "end": v(-53.32, 1.67) * mm});
            skLineSegment(sketch, "E301.MirrorCS", {"start": v(-41.48, -10.39) * mm, "end": v(-39.71, -10.89) * mm, "construction": true});
            skArc(sketch, "E302.MirrorCS", {"start": v(-51.92, -0.41) * mm, "mid": v(-51.72, -0.03) * mm, "end": v(-51.89, 0.37) * mm});
            skArc(sketch, "E303.MirrorCS", {"start": v(-34.91, -11.84) * mm, "mid": v(-34.57, -11.78) * mm, "end": v(-34.35, -11.52) * mm});
            skArc(sketch, "E304.MirrorCS", {"start": v(-62.23, 7.75) * mm, "mid": v(-61.96, 7.52) * mm, "end": v(-61.61, 7.52) * mm});
            skLineSegment(sketch, "E305.MirrorCS", {"start": v(-57.64, 5.96) * mm, "end": v(-59.57, 4) * mm});
            skArc(sketch, "E306.MirrorCS", {"start": v(-3.6, -5.02) * mm, "mid": v(-3.94, -5.11) * mm, "end": v(-4.26, -4.97) * mm});
            skArc(sketch, "E307.MirrorCS", {"start": v(3.07, 6.7) * mm, "mid": v(3.44, 6.92) * mm, "end": v(3.85, 6.77) * mm});
            skLineSegment(sketch, "E308.MirrorCS", {"start": v(-59.05, 2.55) * mm, "end": v(-59.62, 3.36) * mm});
            skArc(sketch, "E309.MirrorCS", {"start": v(-64.99, 15.12) * mm, "mid": v(-65.22, 14.86) * mm, "end": v(-65.22, 14.5) * mm});
            skArc(sketch, "E310.MirrorCS", {"start": v(-1.88, 0.4) * mm, "mid": v(-2.08, 0.78) * mm, "end": v(-1.9, 1.18) * mm});
            skArc(sketch, "E311.MirrorCS", {"start": v(-43.42, -6.13) * mm, "mid": v(-43.36, -5.7) * mm, "end": v(-43.65, -5.38) * mm});
            skLineSegment(sketch, "E312.MirrorCS", {"start": v(-67.08, 20.76) * mm, "end": v(-66.68, 18.97) * mm, "construction": true});
            skLineSegment(sketch, "E313.MirrorCS", {"start": v(-55.79, -1.1) * mm, "end": v(-54.43, -2.35) * mm, "construction": true});
            skLineSegment(sketch, "E314.MirrorCS", {"start": v(8.8, 17.29) * mm, "end": v(11.2, 15.93) * mm});
            skLineSegment(sketch, "E315.MirrorCS", {"start": v(10.53, 14.06) * mm, "end": v(7.83, 14.52) * mm});
            skLineSegment(sketch, "E316.MirrorCS", {"start": v(-22.65, -9.27) * mm, "end": v(-23.03, -12.14) * mm});
            skLineSegment(sketch, "E317.MirrorCS", {"start": v(12.46, 19.8) * mm, "end": v(9.72, 19.93) * mm});
            skLineSegment(sketch, "E318.MirrorCS", {"start": v(-19.45, -10.7) * mm, "end": v(-20.4, -8.13) * mm});
            skLineSegment(sketch, "E319.MirrorCS", {"start": v(-7.67, -4.17) * mm, "end": v(-7.06, -6.84) * mm});
            skLineSegment(sketch, "E320.MirrorCS", {"start": v(4.63, 3.2) * mm, "end": v(2.15, 4.37) * mm});
            skPoint(sketch, "E321.MirrorP", {"position": v(-36.3, -7.82) * mm});
            skLineSegment(sketch, "E322.MirrorCS", {"start": v(-17.5, -7.61) * mm, "end": v(-17.5, -10.35) * mm});
            skLineSegment(sketch, "E323.MirrorCS", {"start": v(-14.27, -9.7) * mm, "end": v(-15.47, -7.22) * mm});
            skLineSegment(sketch, "E324.MirrorCS", {"start": v(-3.82, -1.34) * mm, "end": v(-2.64, -3.81) * mm});
            skPoint(sketch, "E325.MirrorP", {"position": v(-12.32, -9.57) * mm});
            skLineSegment(sketch, "E326.MirrorCS", {"start": v(-24.96, -12.22) * mm, "end": v(-25.75, -8.65) * mm});
            skLineSegment(sketch, "E327.MirrorCS", {"start": v(7.82, 8.34) * mm, "end": v(5.24, 9.28) * mm});
            skLineSegment(sketch, "E328.MirrorCS", {"start": v(-12.64, -6.42) * mm, "end": v(-12.36, -9.15) * mm});
            skPoint(sketch, "E329.MirrorP", {"position": v(-12, -5.7) * mm});
            skPoint(sketch, "E330.MirrorP", {"position": v(-47.15, -3.43) * mm});
            skPoint(sketch, "E331.MirrorP", {"position": v(-38.07, -7.5) * mm});
            skPoint(sketch, "E332.MirrorP", {"position": v(1.99, -0.3) * mm});
            skPoint(sketch, "E333.MirrorP", {"position": v(-58.47, 8.67) * mm});
            skLineSegment(sketch, "E334.MirrorCS", {"start": v(-36.3, -8.42) * mm, "end": v(-36.3, -11.17) * mm});
            skPoint(sketch, "E335.MirrorP", {"position": v(13.92, 24.75) * mm});
            skPoint(sketch, "E336.MirrorP", {"position": v(-51.34, -5) * mm});
            skLineSegment(sketch, "E337.MirrorCS", {"start": v(-49.98, -2.15) * mm, "end": v(-51.16, -4.63) * mm});
            skPoint(sketch, "E338.MirrorP", {"position": v(9.8, 23.03) * mm});
            skPoint(sketch, "E339.MirrorP", {"position": v(9.14, 9.78) * mm});
            skPoint(sketch, "E340.MirrorP", {"position": v(-64.36, 27.2) * mm});
            skPoint(sketch, "E341.MirrorP", {"position": v(11.56, 15.72) * mm});
            skPoint(sketch, "E342.MirrorP", {"position": v(13.29, 21.57) * mm});
            skPoint(sketch, "E343.MirrorP", {"position": v(-23.07, -12.4) * mm});
            skPoint(sketch, "E344.MirrorP", {"position": v(-2.46, -4.2) * mm});
            skPoint(sketch, "E345.MirrorP", {"position": v(6.07, 4.52) * mm});
            skLineSegment(sketch, "E346.MirrorCS", {"start": v(-46.13, -4.98) * mm, "end": v(-46.74, -7.66) * mm});
            skPoint(sketch, "E347.MirrorP", {"position": v(-36.3, -11.6) * mm});
            skPoint(sketch, "E348.MirrorP", {"position": v(-59.87, 3.7) * mm});
            skPoint(sketch, "E349.MirrorP", {"position": v(-67.96, 25.76) * mm});
            skPoint(sketch, "E350.MirrorP", {"position": v(-61.02, 13.8) * mm});
            skLineSegment(sketch, "E351.MirrorCS", {"start": v(-34.35, -11.52) * mm, "end": v(-33.4, -8.94) * mm});
            skPoint(sketch, "E352.MirrorP", {"position": v(-22.57, -8.67) * mm});
            skPoint(sketch, "E353.MirrorP", {"position": v(3.42, 7.2) * mm});
            skPoint(sketch, "E354.MirrorP", {"position": v(-4.08, -0.8) * mm});
            skPoint(sketch, "E355.MirrorP", {"position": v(-12.7, -5.82) * mm});
            skPoint(sketch, "E356.MirrorP", {"position": v(-31.04, -8.74) * mm});
            skPoint(sketch, "E357.MirrorP", {"position": v(-67.08, 20.76) * mm});
            skPoint(sketch, "E358.MirrorP", {"position": v(-49.84, -6.08) * mm});
            skPoint(sketch, "E359.MirrorP", {"position": v(-34.5, -11.92) * mm});
            skLineSegment(sketch, "E360.MirrorCS", {"start": v(-66.25, 18.99) * mm, "end": v(-63.52, 19.11) * mm});
            skPoint(sketch, "E361.MirrorP", {"position": v(-43.1, -5.62) * mm});
            skPoint(sketch, "E362.MirrorP", {"position": v(-65.36, 14.91) * mm});
            skPoint(sketch, "E363.MirrorP", {"position": v(-57.22, 6.39) * mm});
            skLineSegment(sketch, "E364.MirrorCS", {"start": v(-61.61, 7.52) * mm, "end": v(-59.04, 8.46) * mm});
            skPoint(sketch, "E365.MirrorP", {"position": v(-67.71, 23.94) * mm});
            skPoint(sketch, "E366.MirrorP", {"position": v(10.95, 14) * mm});
            skPoint(sketch, "E367.MirrorP", {"position": v(8.22, 8.2) * mm});
            skPoint(sketch, "E368.MirrorP", {"position": v(-19.3, -11.1) * mm});
            skPoint(sketch, "E369.MirrorP", {"position": v(-30.55, -12.48) * mm});
            skPoint(sketch, "E370.MirrorP", {"position": v(-39.71, -10.89) * mm});
            skPoint(sketch, "E371.MirrorP", {"position": v(-45.14, -8.79) * mm});
            skLineSegment(sketch, "E372.MirrorCS", {"start": v(-64.16, 21.98) * mm, "end": v(-66.69, 20.92) * mm});
            skPoint(sketch, "E373.MirrorP", {"position": v(-25.71, -8.8) * mm});
            skPoint(sketch, "E374.MirrorP", {"position": v(-8.66, -7.97) * mm});
            skPoint(sketch, "E375.MirrorP", {"position": v(0.63, -1.54) * mm});
            skLineSegment(sketch, "E376.MirrorCS", {"start": v(-30.96, -9.34) * mm, "end": v(-30.6, -12.06) * mm});
            skPoint(sketch, "E377.MirrorP", {"position": v(1.6, 4.63) * mm});
            skPoint(sketch, "E378.MirrorP", {"position": v(-62.93, 8.97) * mm});
            skPoint(sketch, "E379.MirrorP", {"position": v(-6.64, -2.62) * mm});
            skPoint(sketch, "E380.MirrorP", {"position": v(-15.73, -6.68) * mm});
            skPoint(sketch, "E381.MirrorP", {"position": v(9.11, 19.95) * mm});
            skPoint(sketch, "E382.MirrorP", {"position": v(-41.48, -10.39) * mm});
            skPoint(sketch, "E383.MirrorP", {"position": v(-58.8, 2.2) * mm});
            skPoint(sketch, "E384.MirrorP", {"position": v(-41.79, -6.51) * mm});
            skLineSegment(sketch, "E385.MirrorCS", {"start": v(-64.32, 13.25) * mm, "end": v(-61.62, 13.7) * mm});
            skLineSegment(sketch, "E386.MirrorCS", {"start": v(-28.62, -12.14) * mm, "end": v(-28.03, -9.47) * mm});
            skPoint(sketch, "E387.MirrorP", {"position": v(7.23, 14.62) * mm});
            skPoint(sketch, "E388.MirrorP", {"position": v(4.67, 9.48) * mm});
            skPoint(sketch, "E389.MirrorP", {"position": v(-62.08, 16.77) * mm});
            skPoint(sketch, "E390.MirrorP", {"position": v(-17.78, -6.94) * mm});
            skPoint(sketch, "E391.MirrorP", {"position": v(-10.7, -4.8) * mm});
            skLineSegment(sketch, "E392.MirrorCS", {"start": v(-67.29, 23.92) * mm, "end": v(-64.55, 23.8) * mm});
            skPoint(sketch, "E393.MirrorP", {"position": v(-2.36, 0.77) * mm});
            skPoint(sketch, "E394.MirrorP", {"position": v(-27.5, -8.06) * mm});
            skPoint(sketch, "E395.MirrorP", {"position": v(-55.79, -1.1) * mm});
            skPoint(sketch, "E396.MirrorP", {"position": v(-36.01, -7.75) * mm});
            skPoint(sketch, "E397.MirrorP", {"position": v(-66.68, 18.97) * mm});
            skPoint(sketch, "E398.MirrorP", {"position": v(-60.04, 11.4) * mm});
            skPoint(sketch, "E399.MirrorP", {"position": v(-24.9, -12.48) * mm});
            skPoint(sketch, "E400.MirrorP", {"position": v(5.01, 3.02) * mm});
            skPoint(sketch, "E401.MirrorP", {"position": v(-3.95, -5.27) * mm});
            skPoint(sketch, "E402.MirrorP", {"position": v(-14.09, -10.08) * mm});
            skPoint(sketch, "E403.MirrorP", {"position": v(12.88, 19.78) * mm});
            skPoint(sketch, "E404.MirrorP", {"position": v(-62.91, 19.14) * mm});
            skLineSegment(sketch, "E405.MirrorCS", {"start": v(-41.16, -7.23) * mm, "end": v(-41.44, -9.96) * mm});
            skPoint(sketch, "E406.MirrorP", {"position": v(-42.3, -10.25) * mm});
            skPoint(sketch, "E407.MirrorP", {"position": v(10.56, 28.64) * mm});
            skLineSegment(sketch, "E408.MirrorCS", {"start": v(-64.94, 26.72) * mm, "end": v(-67.55, 25.9) * mm});
            skPoint(sketch, "E409.MirrorP", {"position": v(-28.7, -12.56) * mm});
            skPoint(sketch, "E410.MirrorP", {"position": v(-54.43, -2.35) * mm});
            skPoint(sketch, "E411.MirrorP", {"position": v(-53.77, 2.08) * mm});
            skPoint(sketch, "E412.MirrorP", {"position": v(-64.75, 13.18) * mm});
            skLineSegment(sketch, "E413.MirrorCS", {"start": v(-39.52, -10.5) * mm, "end": v(-38.33, -8.04) * mm});
            skPoint(sketch, "E414.MirrorP", {"position": v(8.28, 17.58) * mm});
            skPoint(sketch, "E415.MirrorP", {"position": v(6.25, 12.2) * mm});
            skPoint(sketch, "E416.MirrorP", {"position": v(9.85, 23.84) * mm});
            skPoint(sketch, "E417.MirrorP", {"position": v(14.16, 26.58) * mm});
            skPoint(sketch, "E418.MirrorP", {"position": v(-17.5, -7) * mm});
            skPoint(sketch, "E419.MirrorP", {"position": v(-41.1, -6.63) * mm});
            skPoint(sketch, "E420.MirrorP", {"position": v(-0.03, 2.9) * mm});
            skPoint(sketch, "E421.MirrorP", {"position": v(-55.4, 3.82) * mm});
            skPoint(sketch, "E422.MirrorP", {"position": v(-63.6, 22.21) * mm});
            skLineSegment(sketch, "E423.MirrorCS", {"start": v(13.5, 24.74) * mm, "end": v(10.75, 24.62) * mm});
            skLineSegment(sketch, "E424.MirrorCS", {"start": v(11.14, 27.53) * mm, "end": v(13.75, 26.7) * mm});
            skPoint(sketch, "E425.MirrorP", {"position": v(-62.01, 7.38) * mm});
            skPoint(sketch, "E426.MirrorP", {"position": v(-11.5, -9.44) * mm});
            skPoint(sketch, "E427.MirrorP", {"position": v(-51.44, -0.04) * mm});
            skPoint(sketch, "E428.MirrorP", {"position": v(-63.65, 23.03) * mm});
            skPoint(sketch, "E429.MirrorP", {"position": v(-17.5, -10.78) * mm});
            skPoint(sketch, "E430.MirrorP", {"position": v(-49.72, -1.6) * mm});
            skLineSegment(sketch, "E431.MirrorCS", {"start": v(13.57, 31.58) * mm, "end": v(13.7, 30.6) * mm});
            skLineSegment(sketch, "E432.MirrorCS", {"start": v(-23.65, 68.42) * mm, "end": v(-25.5, 68.5) * mm, "construction": true});
            skArc(sketch, "E433.MirrorCS", {"start": v(-25.07, 68.48) * mm, "mid": v(-25.4, 68.38) * mm, "end": v(-25.58, 68.09) * mm});
            skLineSegment(sketch, "E434.MirrorCS", {"start": v(-25.07, 68.48) * mm, "end": v(-24.08, 68.44) * mm});
            skArc(sketch, "E435.MirrorCS", {"start": v(1.36, 56.7) * mm, "mid": v(1.43, 57.03) * mm, "end": v(1.27, 57.34) * mm});
            skArc(sketch, "E436.MirrorCS", {"start": v(-23.6, 68) * mm, "mid": v(-23.76, 68.3) * mm, "end": v(-24.08, 68.44) * mm});
            skLineSegment(sketch, "E437.MirrorCS", {"start": v(0.54, 58) * mm, "end": v(1.27, 57.34) * mm});
            skLineSegment(sketch, "E438.MirrorCS", {"start": v(-12.72, 66.33) * mm, "end": v(-14.5, 66.83) * mm, "construction": true});
            skArc(sketch, "E439.MirrorCS", {"start": v(-0.88, 54.27) * mm, "mid": v(-0.47, 54.14) * mm, "end": v(-0.1, 54.37) * mm});
            skLineSegment(sketch, "E440.MirrorCS", {"start": v(11.16, 41.03) * mm, "end": v(10.54, 42.76) * mm, "construction": true});
            skArc(sketch, "E441.MirrorCS", {"start": v(8.03, 48.2) * mm, "mid": v(7.76, 48.42) * mm, "end": v(7.41, 48.42) * mm});
            skArc(sketch, "E442.MirrorCS", {"start": v(-19.29, 67.78) * mm, "mid": v(-19.63, 67.72) * mm, "end": v(-19.85, 67.46) * mm});
            skArc(sketch, "E443.MirrorCS", {"start": v(-3.04, 60.57) * mm, "mid": v(-3, 60.91) * mm, "end": v(-3.2, 61.2) * mm});
            skArc(sketch, "E444.MirrorCS", {"start": v(10.79, 40.82) * mm, "mid": v(11.01, 41.09) * mm, "end": v(11.02, 41.43) * mm});
            skLineSegment(sketch, "E445.MirrorCS", {"start": v(4.85, 53.39) * mm, "end": v(5.42, 52.58) * mm});
            skLineSegment(sketch, "E446.MirrorCS", {"start": v(-19.29, 67.78) * mm, "end": v(-18.32, 67.6) * mm});
            skLineSegment(sketch, "E447.MirrorCS", {"start": v(-6.56, 59.02) * mm, "end": v(-4.98, 57.9) * mm});
            skLineSegment(sketch, "E448.MirrorCS", {"start": v(5.67, 52.24) * mm, "end": v(4.6, 53.74) * mm, "construction": true});
            skArc(sketch, "E449.MirrorCS", {"start": v(-17.9, 67.1) * mm, "mid": v(-18.02, 67.44) * mm, "end": v(-18.32, 67.6) * mm});
            skArc(sketch, "E450.MirrorCS", {"start": v(-6.62, 59.8) * mm, "mid": v(-6.77, 59.4) * mm, "end": v(-6.56, 59.02) * mm});
            skLineSegment(sketch, "E451.MirrorCS", {"start": v(8.84, 36.2) * mm, "end": v(9.27, 34.32) * mm});
            skArc(sketch, "E452.MirrorCS", {"start": v(-26.17, 65.4) * mm, "mid": v(-26.08, 64.99) * mm, "end": v(-25.7, 64.8) * mm});
            skArc(sketch, "E453.MirrorCS", {"start": v(7.42, 42.24) * mm, "mid": v(7.07, 42) * mm, "end": v(7.03, 41.57) * mm});
            skArc(sketch, "E454.MirrorCS", {"start": v(-14.08, 66.71) * mm, "mid": v(-14.43, 66.69) * mm, "end": v(-14.68, 66.45) * mm});
            skArc(sketch, "E455.MirrorCS", {"start": v(10.35, 32.13) * mm, "mid": v(9.95, 31.97) * mm, "end": v(9.82, 31.56) * mm});
            skLineSegment(sketch, "E456.MirrorCS", {"start": v(8.03, 48.2) * mm, "end": v(8.52, 47.34) * mm});
            skArc(sketch, "E457.MirrorCS", {"start": v(10.69, 42.36) * mm, "mid": v(10.47, 42.63) * mm, "end": v(10.12, 42.7) * mm});
            skArc(sketch, "E458.MirrorCS", {"start": v(13.35, 30.05) * mm, "mid": v(13.62, 30.26) * mm, "end": v(13.7, 30.6) * mm});
            skArc(sketch, "E459.MirrorCS", {"start": v(4.85, 53.39) * mm, "mid": v(4.57, 53.59) * mm, "end": v(4.22, 53.55) * mm});
            skArc(sketch, "E460.MirrorCS", {"start": v(9.31, 36.83) * mm, "mid": v(8.93, 36.63) * mm, "end": v(8.84, 36.2) * mm});
            skArc(sketch, "E461.MirrorCS", {"start": v(-4.98, 57.9) * mm, "mid": v(-4.55, 57.82) * mm, "end": v(-4.22, 58.1) * mm});
            skArc(sketch, "E462.MirrorCS", {"start": v(8.4, 46.7) * mm, "mid": v(8.58, 47) * mm, "end": v(8.52, 47.34) * mm});
            skLineSegment(sketch, "E463.MirrorCS", {"start": v(-7.37, 64.01) * mm, "end": v(-9.06, 64.73) * mm, "construction": true});
            skLineSegment(sketch, "E464.MirrorCS", {"start": v(-10.55, 61.32) * mm, "end": v(-8.76, 60.57) * mm});
            skLineSegment(sketch, "E465.MirrorCS", {"start": v(1.54, 51.63) * mm, "end": v(2.67, 50.05) * mm});
            skArc(sketch, "E466.MirrorCS", {"start": v(-4, 61.77) * mm, "mid": v(-4.34, 61.86) * mm, "end": v(-4.66, 61.72) * mm});
            skLineSegment(sketch, "E467.MirrorCS", {"start": v(9.82, 31.56) * mm, "end": v(10.08, 29.64) * mm});
            skArc(sketch, "E468.MirrorCS", {"start": v(-13.69, 62.74) * mm, "mid": v(-13.26, 62.8) * mm, "end": v(-13.04, 63.18) * mm});
            skArc(sketch, "E469.MirrorCS", {"start": v(13.57, 31.58) * mm, "mid": v(13.4, 31.89) * mm, "end": v(13.09, 32.02) * mm});
            skArc(sketch, "E470.MirrorCS", {"start": v(1.74, 52.38) * mm, "mid": v(1.47, 52.05) * mm, "end": v(1.54, 51.63) * mm});
            skLineSegment(sketch, "E471.MirrorCS", {"start": v(7.03, 41.57) * mm, "end": v(7.67, 39.74) * mm});
            skLineSegment(sketch, "E472.MirrorCS", {"start": v(8.73, 46.97) * mm, "end": v(7.81, 48.56) * mm, "construction": true});
            skLineSegment(sketch, "E473.MirrorCS", {"start": v(-4, 61.77) * mm, "end": v(-3.2, 61.2) * mm});
            skLineSegment(sketch, "E474.MirrorCS", {"start": v(-15.55, 63.27) * mm, "end": v(-13.69, 62.74) * mm});
            skLineSegment(sketch, "E475.MirrorCS", {"start": v(-2.31, 55.58) * mm, "end": v(-0.88, 54.27) * mm});
            skArc(sketch, "E476.MirrorCS", {"start": v(-10.78, 62.07) * mm, "mid": v(-10.84, 61.64) * mm, "end": v(-10.55, 61.32) * mm});
            skLineSegment(sketch, "E477.MirrorCS", {"start": v(12.88, 35.18) * mm, "end": v(12.48, 36.98) * mm, "construction": true});
            skArc(sketch, "E478.MirrorCS", {"start": v(9.27, 34.32) * mm, "mid": v(9.53, 33.98) * mm, "end": v(9.96, 33.96) * mm});
            skArc(sketch, "E479.MirrorCS", {"start": v(-15.87, 63.98) * mm, "mid": v(-15.88, 63.55) * mm, "end": v(-15.55, 63.27) * mm});
            skArc(sketch, "E480.MirrorCS", {"start": v(5.54, 45.07) * mm, "mid": v(5.9, 44.82) * mm, "end": v(6.3, 44.93) * mm});
            skArc(sketch, "E481.MirrorCS", {"start": v(12.49, 35.02) * mm, "mid": v(12.74, 35.25) * mm, "end": v(12.79, 35.6) * mm});
            skArc(sketch, "E482.MirrorCS", {"start": v(10.08, 29.64) * mm, "mid": v(10.3, 29.28) * mm, "end": v(10.73, 29.22) * mm});
            skArc(sketch, "E483.MirrorCS", {"start": v(7.67, 39.74) * mm, "mid": v(7.98, 39.43) * mm, "end": v(8.4, 39.47) * mm});
            skArc(sketch, "E484.MirrorCS", {"start": v(-18.5, 63.87) * mm, "mid": v(-18.09, 63.98) * mm, "end": v(-17.9, 64.37) * mm});
            skLineSegment(sketch, "E485.MirrorCS", {"start": v(10.69, 42.36) * mm, "end": v(11.02, 41.43) * mm});
            skLineSegment(sketch, "E486.MirrorCS", {"start": v(-8.67, 64.56) * mm, "end": v(-7.76, 64.18) * mm});
            skArc(sketch, "E487.MirrorCS", {"start": v(0.54, 58) * mm, "mid": v(0.22, 58.13) * mm, "end": v(-0.11, 58.03) * mm});
            skArc(sketch, "E488.MirrorCS", {"start": v(-12.76, 65.9) * mm, "mid": v(-12.85, 66.24) * mm, "end": v(-13.13, 66.44) * mm});
            skLineSegment(sketch, "E489.MirrorCS", {"start": v(-14.08, 66.71) * mm, "end": v(-13.13, 66.44) * mm});
            skLineSegment(sketch, "E490.MirrorCS", {"start": v(-17.9, 67.53) * mm, "end": v(-19.7, 67.86) * mm, "construction": true});
            skLineSegment(sketch, "E491.MirrorCS", {"start": v(1.58, 57.05) * mm, "end": v(0.23, 58.29) * mm, "construction": true});
            skLineSegment(sketch, "E492.MirrorCS", {"start": v(12.57, 36.56) * mm, "end": v(12.79, 35.6) * mm});
            skArc(sketch, "E493.MirrorCS", {"start": v(-8.67, 64.56) * mm, "mid": v(-9.02, 64.58) * mm, "end": v(-9.3, 64.37) * mm});
            skArc(sketch, "E494.MirrorCS", {"start": v(-20.8, 64.88) * mm, "mid": v(-20.76, 64.46) * mm, "end": v(-20.41, 64.2) * mm});
            skArc(sketch, "E495.MirrorCS", {"start": v(5.37, 51.93) * mm, "mid": v(5.51, 52.25) * mm, "end": v(5.42, 52.58) * mm});
            skArc(sketch, "E496.MirrorCS", {"start": v(4.84, 47.48) * mm, "mid": v(4.53, 47.18) * mm, "end": v(4.57, 46.75) * mm});
            skArc(sketch, "E497.MirrorCS", {"start": v(-7.46, 63.6) * mm, "mid": v(-7.5, 63.94) * mm, "end": v(-7.76, 64.18) * mm});
            skArc(sketch, "E498.MirrorCS", {"start": v(-8.76, 60.57) * mm, "mid": v(-8.34, 60.59) * mm, "end": v(-8.07, 60.93) * mm});
            skLineSegment(sketch, "E499.MirrorCS", {"start": v(4.57, 46.75) * mm, "end": v(5.54, 45.07) * mm});
            skLineSegment(sketch, "E500.MirrorCS", {"start": v(13.75, 30.18) * mm, "end": v(13.51, 32) * mm, "construction": true});
            skArc(sketch, "E501.MirrorCS", {"start": v(12.57, 36.56) * mm, "mid": v(12.39, 36.85) * mm, "end": v(12.05, 36.96) * mm});
            skArc(sketch, "E502.MirrorCS", {"start": v(-2.28, 56.35) * mm, "mid": v(-2.48, 55.97) * mm, "end": v(-2.31, 55.58) * mm});
            skArc(sketch, "E503.MirrorCS", {"start": v(2.67, 50.05) * mm, "mid": v(3.04, 49.83) * mm, "end": v(3.44, 49.98) * mm});
            skArc(sketch, "E504.MirrorCS", {"start": v(-23.76, 64.7) * mm, "mid": v(-23.37, 64.87) * mm, "end": v(-23.24, 65.28) * mm});
            skLineSegment(sketch, "E505.MirrorCS", {"start": v(-20.41, 64.2) * mm, "end": v(-18.5, 63.87) * mm});
            skPoint(sketch, "E506.MirrorP", {"position": v(-17.9, 63.76) * mm});
            skPoint(sketch, "E507.MirrorP", {"position": v(9.4, 33.73) * mm});
            skLineSegment(sketch, "E508.MirrorCS", {"start": v(-14.68, 66.45) * mm, "end": v(-15.87, 63.98) * mm});
            skPoint(sketch, "E509.MirrorP", {"position": v(7.88, 39.17) * mm});
            skPoint(sketch, "E510.MirrorP", {"position": v(-7.05, 59.37) * mm});
            skPoint(sketch, "E511.MirrorP", {"position": v(7.81, 48.56) * mm});
            skLineSegment(sketch, "E512.MirrorCS", {"start": v(-9.3, 64.37) * mm, "end": v(-10.78, 62.07) * mm});
            skLineSegment(sketch, "E513.MirrorCS", {"start": v(3.44, 49.98) * mm, "end": v(5.37, 51.93) * mm});
            skPoint(sketch, "E514.MirrorP", {"position": v(9.45, 32.91) * mm});
            skPoint(sketch, "E515.MirrorP", {"position": v(-16.14, 63.43) * mm});
            skPoint(sketch, "E516.MirrorP", {"position": v(10.54, 42.76) * mm});
            skLineSegment(sketch, "E517.MirrorCS", {"start": v(-0.1, 54.37) * mm, "end": v(1.36, 56.7) * mm});
            skLineSegment(sketch, "E518.MirrorCS", {"start": v(-25.7, 64.8) * mm, "end": v(-23.76, 64.7) * mm});
            skLineSegment(sketch, "E519.MirrorCS", {"start": v(10.73, 29.22) * mm, "end": v(13.35, 30.05) * mm});
            skPoint(sketch, "E520.MirrorP", {"position": v(11.16, 41.03) * mm});
            skPoint(sketch, "E521.MirrorP", {"position": v(-23.16, 64.68) * mm});
            skPoint(sketch, "E522.MirrorP", {"position": v(-0.43, 53.86) * mm});
            skPoint(sketch, "E523.MirrorP", {"position": v(-25.5, 68.5) * mm});
            skPoint(sketch, "E524.MirrorP", {"position": v(0.23, 58.29) * mm});
            skPoint(sketch, "E525.MirrorP", {"position": v(-11.1, 61.56) * mm});
            skLineSegment(sketch, "E526.MirrorCS", {"start": v(8.4, 39.47) * mm, "end": v(10.79, 40.82) * mm});
            skLineSegment(sketch, "E527.MirrorCS", {"start": v(13.09, 32.02) * mm, "end": v(10.35, 32.13) * mm});
            skPoint(sketch, "E528.MirrorP", {"position": v(5.84, 44.54) * mm});
            skPoint(sketch, "E529.MirrorP", {"position": v(12.48, 36.98) * mm});
            skPoint(sketch, "E530.MirrorP", {"position": v(-18.19, 63.69) * mm});
            skLineSegment(sketch, "E531.MirrorCS", {"start": v(-0.11, 58.03) * mm, "end": v(-2.28, 56.35) * mm});
            skLineSegment(sketch, "E532.MirrorCS", {"start": v(-4.66, 61.72) * mm, "end": v(-6.62, 59.8) * mm});
            skLineSegment(sketch, "E533.MirrorCS", {"start": v(10.12, 42.7) * mm, "end": v(7.42, 42.24) * mm});
            skPoint(sketch, "E534.MirrorP", {"position": v(-12.72, 66.33) * mm});
            skPoint(sketch, "E535.MirrorP", {"position": v(-12.41, 62.46) * mm});
            skPoint(sketch, "E536.MirrorP", {"position": v(4.6, 53.74) * mm});
            skLineSegment(sketch, "E537.MirrorCS", {"start": v(9.96, 33.96) * mm, "end": v(12.49, 35.02) * mm});
            skLineSegment(sketch, "E538.MirrorCS", {"start": v(7.41, 48.42) * mm, "end": v(4.84, 47.48) * mm});
            skPoint(sketch, "E539.MirrorP", {"position": v(-23.65, 68.42) * mm});
            skPoint(sketch, "E540.MirrorP", {"position": v(-9.06, 64.73) * mm});
            skPoint(sketch, "E541.MirrorP", {"position": v(-14.5, 66.83) * mm});
            skPoint(sketch, "E542.MirrorP", {"position": v(13.51, 32) * mm});
            skPoint(sketch, "E543.MirrorP", {"position": v(3.02, 49.55) * mm});
            skLineSegment(sketch, "E544.MirrorCS", {"start": v(12.05, 36.96) * mm, "end": v(9.31, 36.83) * mm});
            skPoint(sketch, "E545.MirrorP", {"position": v(12.88, 35.18) * mm});
            skPoint(sketch, "E546.MirrorP", {"position": v(-19.7, 67.86) * mm});
            skPoint(sketch, "E547.MirrorP", {"position": v(-4.36, 62.02) * mm});
            skLineSegment(sketch, "E548.MirrorCS", {"start": v(6.3, 44.93) * mm, "end": v(8.4, 46.7) * mm});
            skLineSegment(sketch, "E549.MirrorCS", {"start": v(-19.85, 67.46) * mm, "end": v(-20.8, 64.88) * mm});
            skPoint(sketch, "E550.MirrorP", {"position": v(5.67, 52.24) * mm});
            skPoint(sketch, "E551.MirrorP", {"position": v(6.82, 42.14) * mm});
            skPoint(sketch, "E552.MirrorP", {"position": v(13.75, 30.18) * mm});
            skLineSegment(sketch, "E553.MirrorCS", {"start": v(-17.9, 64.37) * mm, "end": v(-17.9, 67.1) * mm});
            skPoint(sketch, "E554.MirrorP", {"position": v(-4.48, 57.55) * mm});
            skPoint(sketch, "E555.MirrorP", {"position": v(4.27, 47.27) * mm});
            skPoint(sketch, "E556.MirrorP", {"position": v(-2.86, 60.95) * mm});
            skLineSegment(sketch, "E557.MirrorCS", {"start": v(4.22, 53.55) * mm, "end": v(1.74, 52.38) * mm});
            skLineSegment(sketch, "E558.MirrorCS", {"start": v(-8.07, 60.93) * mm, "end": v(-7.46, 63.6) * mm});
            skPoint(sketch, "E559.MirrorP", {"position": v(-13.1, 62.57) * mm});
            skPoint(sketch, "E560.MirrorP", {"position": v(-2.76, 55.98) * mm});
            skPoint(sketch, "E561.MirrorP", {"position": v(-17.9, 67.53) * mm});
            skLineSegment(sketch, "E562.MirrorCS", {"start": v(-23.24, 65.28) * mm, "end": v(-23.6, 68) * mm});
            skPoint(sketch, "E563.MirrorP", {"position": v(8.73, 46.97) * mm});
            skLineSegment(sketch, "E564.MirrorCS", {"start": v(-25.58, 68.09) * mm, "end": v(-26.17, 65.4) * mm});
            skPoint(sketch, "E565.MirrorP", {"position": v(1.58, 57.05) * mm});
            skPoint(sketch, "E566.MirrorP", {"position": v(-26.3, 63.9) * mm});
            skPoint(sketch, "E567.MirrorP", {"position": v(-11.9, 66.2) * mm});
            skPoint(sketch, "E568.MirrorP", {"position": v(8.71, 36.8) * mm});
            skLineSegment(sketch, "E569.MirrorCS", {"start": v(-4.22, 58.1) * mm, "end": v(-3.04, 60.57) * mm});
            skLineSegment(sketch, "E570.MirrorCS", {"start": v(-13.04, 63.18) * mm, "end": v(-12.76, 65.9) * mm});
            skPoint(sketch, "E571.MirrorP", {"position": v(1.2, 52.12) * mm});
            skSolve(sketch);
        }
        {
            var Q0;
            {var subQ0=sQuery(id+"F0.wireOp",EDGE,"0311cbe4-9802-47d4-9d7a-323a3fcd4f84");Q0=makeQuery(id+"F0.imprint","IMPRINT",FACE,{"disambiguationData":[TD([[makeQuery(id+"F0.imprint","IMPRINT",EDGE,{"derivedFrom":subQ0}),1.0]])]});}
            var Q1;
            Q1=makeQuery(id+"F0.imprint","IMPRINT",FACE,{"disambiguationData":[TD([[makeQuery(id+"F0.imprint","IMPRINT",EDGE,{"derivedFrom":sQuery(id+"F0.wireOp",EDGE,"6Y6yVGsE-Qq5h-VfEu-5cPj-ENFIb0fyp3xN")}),-1.0]])]});
            var Q2;
            Q2=makeQuery(id+"F0.imprint","IMPRINT",FACE,{"disambiguationData":[TD([[makeQuery(id+"F0.imprint","IMPRINT",EDGE,{"derivedFrom":sQuery(id+"F0.wireOp",EDGE,"0e17b10f-8326-4532-838f-33bf33fb0701")}),-1.0]])]});
            var Q3;
            {var subQ4=sQuery(id+"F0.wireOp",EDGE,"69063c51-fa6a-4bcb-b3ef-7ac22f9e600f");Q3=makeQuery(id+"F0.imprint","IMPRINT",FACE,{"disambiguationData":[TD([[makeQuery(id+"F0.imprint","IMPRINT",EDGE,{"derivedFrom":subQ4}),1.0]])]});}
            var Q4;
            Q4=makeQuery(id+"F0.imprint","IMPRINT",FACE,{"disambiguationData":[TD([[makeQuery(id+"F0.imprint","IMPRINT",EDGE,{"derivedFrom":sQuery(id+"F0.wireOp",EDGE,"9ed62011-bcde-44f3-afe0-c0b80041e9d1")}),-1.0]])]});
            var Q5;
            Q5=makeQuery(id+"F0.imprint","IMPRINT",FACE,{"disambiguationData":[TD([[makeQuery(id+"F0.imprint","IMPRINT",EDGE,{"derivedFrom":sQuery(id+"F0.wireOp",EDGE,"e8fbcba2-6c95-4f4b-8228-5f63cf018b1a")}),-1.0]])]});
            var Q6;
            Q6=makeQuery(id+"F0.imprint","IMPRINT",FACE,{"disambiguationData":[TD([[makeQuery(id+"F0.imprint","IMPRINT",EDGE,{"derivedFrom":sQuery(id+"F0.wireOp",EDGE,"15954d39-2489-47e7-a030-dd86023081a9")}),-1.0]])]});
            var Q7;
            Q7=makeQuery(id+"F0.imprint","IMPRINT",FACE,{"disambiguationData":[TD([[makeQuery(id+"F0.imprint","IMPRINT",EDGE,{"derivedFrom":sQuery(id+"F0.wireOp",EDGE,"645e2f8d-9285-4749-8aa9-a81e661e4867")}),-1.0]])]});
            var Q8;
            Q8=makeQuery(id+"F0.imprint","IMPRINT",FACE,{"disambiguationData":[TD([[makeQuery(id+"F0.imprint","IMPRINT",EDGE,{"derivedFrom":sQuery(id+"F0.wireOp",EDGE,"da72fb55-855e-47ef-a650-d17c736f3d0b")}),-1.0]])]});
            var Q9;
            Q9=makeQuery(id+"F0.imprint","IMPRINT",FACE,{"disambiguationData":[TD([[makeQuery(id+"F0.imprint","IMPRINT",EDGE,{"derivedFrom":sQuery(id+"F0.wireOp",EDGE,"0bad413a-7f9d-45df-b4f7-f9623c414056")}),-1.0]])]});
            var Q10;
            Q10=makeQuery(id+"F0.imprint","IMPRINT",FACE,{"disambiguationData":[TD([[makeQuery(id+"F0.imprint","IMPRINT",EDGE,{"derivedFrom":sQuery(id+"F0.wireOp",EDGE,"7d00cad5-fac4-4050-b715-21e8bdcc284b1.MirrorCS")}),1.0]])]});
            var Q11;
            Q11=makeQuery(id+"F0.imprint","IMPRINT",FACE,{"disambiguationData":[TD([[makeQuery(id+"F0.imprint","IMPRINT",EDGE,{"derivedFrom":sQuery(id+"F0.wireOp",EDGE,"7d00cad5-fac4-4050-b715-21e8bdcc284b10.MirrorCS")}),1.0]])]});
            var Q12;
            Q12=makeQuery(id+"F0.imprint","IMPRINT",FACE,{"disambiguationData":[TD([[makeQuery(id+"F0.imprint","IMPRINT",EDGE,{"derivedFrom":sQuery(id+"F0.wireOp",EDGE,"7d00cad5-fac4-4050-b715-21e8bdcc284b0.MirrorCS")}),1.0]])]});
            var Q13;
            {var subQ4=sQuery(id+"F0.wireOp",EDGE,"7d00cad5-fac4-4050-b715-21e8bdcc284b4.MirrorCS");Q13=makeQuery(id+"F0.imprint","IMPRINT",FACE,{"disambiguationData":[TD([[makeQuery(id+"F0.imprint","IMPRINT",EDGE,{"derivedFrom":subQ4}),-1.0]])]});}
            var Q14;
            {var subQ0=sQuery(id+"F0.wireOp",EDGE,"7d00cad5-fac4-4050-b715-21e8bdcc284b18.MirrorCS");Q14=makeQuery(id+"F0.imprint","IMPRINT",FACE,{"disambiguationData":[TD([[makeQuery(id+"F0.imprint","IMPRINT",EDGE,{"derivedFrom":subQ0}),-1.0]])]});}
            var Q15;
            Q15=makeQuery(id+"F0.imprint","IMPRINT",FACE,{"disambiguationData":[TD([[makeQuery(id+"F0.imprint","IMPRINT",EDGE,{"derivedFrom":sQuery(id+"F0.wireOp",EDGE,"7d00cad5-fac4-4050-b715-21e8bdcc284b11.MirrorCS")}),1.0]])]});
            var Q16;
            Q16=makeQuery(id+"F0.imprint","IMPRINT",FACE,{"disambiguationData":[TD([[makeQuery(id+"F0.imprint","IMPRINT",EDGE,{"derivedFrom":sQuery(id+"F0.wireOp",EDGE,"7d00cad5-fac4-4050-b715-21e8bdcc284b5.MirrorCS")}),-1.0]])]});
            var Q17;
            Q17=makeQuery(id+"F0.imprint","IMPRINT",FACE,{"disambiguationData":[TD([[makeQuery(id+"F0.imprint","IMPRINT",EDGE,{"derivedFrom":sQuery(id+"F0.wireOp",EDGE,"7d00cad5-fac4-4050-b715-21e8bdcc284b3.MirrorCS")}),1.0]])]});
            var Q18;
            Q18=makeQuery(id+"F0.imprint","IMPRINT",FACE,{"disambiguationData":[TD([[makeQuery(id+"F0.imprint","IMPRINT",EDGE,{"derivedFrom":sQuery(id+"F0.wireOp",EDGE,"7d00cad5-fac4-4050-b715-21e8bdcc284b2.MirrorCS")}),1.0]])]});
            var Q19;
            Q19=makeQuery(id+"F0.imprint","IMPRINT",FACE,{"disambiguationData":[TD([[makeQuery(id+"F0.imprint","IMPRINT",EDGE,{"derivedFrom":sQuery(id+"F0.wireOp",EDGE,"7d00cad5-fac4-4050-b715-21e8bdcc284b16.MirrorCS")}),-1.0]])]});
            var Q20;
            Q20=makeQuery(id+"F0.imprint","IMPRINT",FACE,{"disambiguationData":[TD([[makeQuery(id+"F0.imprint","IMPRINT",EDGE,{"derivedFrom":sQuery(id+"F0.wireOp",EDGE,"83a64bb6-06e1-48cd-aad0-cc63c7a6108e32.MirrorCS")}),-1.0]])]});
            var Q21;
            Q21=makeQuery(id+"F0.imprint","IMPRINT",FACE,{"disambiguationData":[TD([[makeQuery(id+"F0.imprint","IMPRINT",EDGE,{"derivedFrom":sQuery(id+"F0.wireOp",EDGE,"83a64bb6-06e1-48cd-aad0-cc63c7a6108e72.MirrorCS")}),-1.0]])]});
            var Q22;
            Q22=makeQuery(id+"F0.imprint","IMPRINT",FACE,{"disambiguationData":[TD([[makeQuery(id+"F0.imprint","IMPRINT",EDGE,{"derivedFrom":sQuery(id+"F0.wireOp",EDGE,"83a64bb6-06e1-48cd-aad0-cc63c7a6108e9.MirrorCS")}),-1.0]])]});
            var Q23;
            {var subQ4=sQuery(id+"F0.wireOp",EDGE,"83a64bb6-06e1-48cd-aad0-cc63c7a6108e16.MirrorCS");Q23=makeQuery(id+"F0.imprint","IMPRINT",FACE,{"disambiguationData":[TD([[makeQuery(id+"F0.imprint","IMPRINT",EDGE,{"derivedFrom":subQ4}),1.0]])]});}
            var Q24;
            {var subQ1=sQuery(id+"F0.wireOp",EDGE,"83a64bb6-06e1-48cd-aad0-cc63c7a6108e88.MirrorCS");Q24=makeQuery(id+"F0.imprint","IMPRINT",FACE,{"disambiguationData":[TD([[makeQuery(id+"F0.imprint","IMPRINT",EDGE,{"derivedFrom":subQ1}),1.0]])]});}
            var Q25;
            {var subQ5=sQuery(id+"F0.wireOp",EDGE,"83a64bb6-06e1-48cd-aad0-cc63c7a6108e73.MirrorCS");Q25=makeQuery(id+"F0.imprint","IMPRINT",FACE,{"disambiguationData":[TD([[makeQuery(id+"F0.imprint","IMPRINT",EDGE,{"derivedFrom":subQ5}),1.0]])]});}
            var Q26;
            {var subQ4=sQuery(id+"F0.wireOp",EDGE,"83a64bb6-06e1-48cd-aad0-cc63c7a6108e22.MirrorCS");Q26=makeQuery(id+"F0.imprint","IMPRINT",FACE,{"disambiguationData":[TD([[makeQuery(id+"F0.imprint","IMPRINT",EDGE,{"derivedFrom":subQ4}),1.0]])]});}
            var Q27;
            {var subQ5=sQuery(id+"F0.wireOp",EDGE,"83a64bb6-06e1-48cd-aad0-cc63c7a6108e15.MirrorCS");Q27=makeQuery(id+"F0.imprint","IMPRINT",FACE,{"disambiguationData":[TD([[makeQuery(id+"F0.imprint","IMPRINT",EDGE,{"derivedFrom":subQ5}),1.0]])]});}
            var Q28;
            {var subQ1=sQuery(id+"F0.wireOp",EDGE,"83a64bb6-06e1-48cd-aad0-cc63c7a6108e4.MirrorCS");Q28=makeQuery(id+"F0.imprint","IMPRINT",FACE,{"disambiguationData":[TD([[makeQuery(id+"F0.imprint","IMPRINT",EDGE,{"derivedFrom":subQ1}),1.0]])]});}
            var Q29;
            Q29=makeQuery(id+"F0.imprint","IMPRINT",FACE,{"disambiguationData":[TD([[makeQuery(id+"F0.imprint","IMPRINT",EDGE,{"derivedFrom":sQuery(id+"F0.wireOp",EDGE,"83a64bb6-06e1-48cd-aad0-cc63c7a6108e1.MirrorCS")}),-1.0]])]});
            var Q30;
            Q30=makeQuery(id+"F0.imprint","IMPRINT",FACE,{"disambiguationData":[TD([[makeQuery(id+"F0.imprint","IMPRINT",EDGE,{"derivedFrom":sQuery(id+"F0.wireOp",EDGE,"83a64bb6-06e1-48cd-aad0-cc63c7a6108e13.MirrorCS")}),1.0]])]});
            var Q31;
            Q31=makeQuery(id+"F0.imprint","IMPRINT",FACE,{"disambiguationData":[TD([[makeQuery(id+"F0.imprint","IMPRINT",EDGE,{"derivedFrom":sQuery(id+"F0.wireOp",EDGE,"83a64bb6-06e1-48cd-aad0-cc63c7a6108e3.MirrorCS")}),1.0]])]});
            var Q32;
            {var subQ4=sQuery(id+"F0.wireOp",EDGE,"83a64bb6-06e1-48cd-aad0-cc63c7a6108e7.MirrorCS");Q32=makeQuery(id+"F0.imprint","IMPRINT",FACE,{"disambiguationData":[TD([[makeQuery(id+"F0.imprint","IMPRINT",EDGE,{"derivedFrom":subQ4}),-1.0]])]});}
            var Q33;
            Q33=makeQuery(id+"F0.imprint","IMPRINT",FACE,{"disambiguationData":[TD([[makeQuery(id+"F0.imprint","IMPRINT",EDGE,{"derivedFrom":sQuery(id+"F0.wireOp",EDGE,"83a64bb6-06e1-48cd-aad0-cc63c7a6108e125.MirrorCS")}),1.0]])]});
            var Q34;
            Q34=makeQuery(id+"F0.imprint","IMPRINT",FACE,{"disambiguationData":[TD([[makeQuery(id+"F0.imprint","IMPRINT",EDGE,{"derivedFrom":sQuery(id+"F0.wireOp",EDGE,"83a64bb6-06e1-48cd-aad0-cc63c7a6108e18.MirrorCS")}),1.0]])]});
            var Q35;
            {var subQ1=sQuery(id+"F0.wireOp",EDGE,"83a64bb6-06e1-48cd-aad0-cc63c7a6108e26.MirrorCS");Q35=makeQuery(id+"F0.imprint","IMPRINT",FACE,{"disambiguationData":[TD([[makeQuery(id+"F0.imprint","IMPRINT",EDGE,{"derivedFrom":subQ1}),-1.0]])]});}
            var Q36;
            Q36=makeQuery(id+"F0.imprint","IMPRINT",FACE,{"disambiguationData":[TD([[makeQuery(id+"F0.imprint","IMPRINT",EDGE,{"derivedFrom":sQuery(id+"F0.wireOp",EDGE,"83a64bb6-06e1-48cd-aad0-cc63c7a6108e20.MirrorCS")}),1.0]])]});
            var Q37;
            Q37=makeQuery(id+"F0.imprint","IMPRINT",FACE,{"disambiguationData":[TD([[makeQuery(id+"F0.imprint","IMPRINT",EDGE,{"derivedFrom":sQuery(id+"F0.wireOp",EDGE,"83a64bb6-06e1-48cd-aad0-cc63c7a6108e11.MirrorCS")}),1.0]])]});
            var Q38;
            Q38=makeQuery(id+"F0.imprint","IMPRINT",FACE,{"disambiguationData":[TD([[makeQuery(id+"F0.imprint","IMPRINT",EDGE,{"derivedFrom":sQuery(id+"F0.wireOp",EDGE,"83a64bb6-06e1-48cd-aad0-cc63c7a6108e0.MirrorCS")}),1.0]])]});
            var Q39;
            {var subQ4=sQuery(id+"F0.wireOp",EDGE,"96c2385a-0bdc-42bc-a880-ad600b45b9f6");Q39=makeQuery(id+"F0.imprint","IMPRINT",FACE,{"disambiguationData":[TD([[makeQuery(id+"F0.imprint","IMPRINT",EDGE,{"derivedFrom":subQ4}),1.0]])]});}
            var Q40;
            Q40=makeQuery(id+"F0.imprint","IMPRINT",FACE,{"disambiguationData":[TD([[makeQuery(id+"F0.imprint","IMPRINT",EDGE,{"derivedFrom":sQuery(id+"F0.wireOp",EDGE,"nPf0oKgk-ypsu-m3Pe-agjd-FQvZDOTVO4sS")}),1.0]])]});
            var Q41;
            Q41=makeQuery(id+"F0.imprint","IMPRINT",FACE,{"disambiguationData":[TD([[makeQuery(id+"F0.imprint","IMPRINT",EDGE,{"derivedFrom":sQuery(id+"F0.wireOp",EDGE,"ae4013c6-7629-4567-bef2-92f7e71cc9b4")}),1.0]])]});
            var Q42;
            {var subQ1=sQuery(id+"F0.wireOp",EDGE,"8eadad72-ae03-40d5-a669-069470c9e60d");Q42=makeQuery(id+"F0.imprint","IMPRINT",FACE,{"disambiguationData":[TD([[makeQuery(id+"F0.imprint","IMPRINT",EDGE,{"derivedFrom":subQ1}),1.0]])]});}
            var Q43;
            Q43=makeQuery(id+"F0.imprint","IMPRINT",FACE,{"disambiguationData":[TD([[makeQuery(id+"F0.imprint","IMPRINT",EDGE,{"derivedFrom":sQuery(id+"F0.wireOp",EDGE,"59916fda-641c-4a45-aded-585673b77d0f")}),1.0]])]});
            var Q44;
            Q44=makeQuery(id+"F0.imprint","IMPRINT",FACE,{"disambiguationData":[TD([[makeQuery(id+"F0.imprint","IMPRINT",EDGE,{"derivedFrom":sQuery(id+"F0.wireOp",EDGE,"c1f97d91-4148-4444-a410-e6df2ce09c54")}),1.0]])]});
            var Q45;
            Q45=makeQuery(id+"F0.imprint","IMPRINT",FACE,{"disambiguationData":[TD([[makeQuery(id+"F0.imprint","IMPRINT",EDGE,{"derivedFrom":sQuery(id+"F0.wireOp",EDGE,"4e4fc5e1-dc05-4d30-b686-c3e83eaca7c8")}),1.0]])]});
            var Q46;
            Q46=makeQuery(id+"F0.imprint","IMPRINT",FACE,{"disambiguationData":[TD([[makeQuery(id+"F0.imprint","IMPRINT",EDGE,{"derivedFrom":sQuery(id+"F0.wireOp",EDGE,"813cdded-b1c8-4a28-9ebd-ed6ade36abff")}),1.0]])]});
            var Q47;
            Q47=makeQuery(id+"F0.imprint","IMPRINT",FACE,{"disambiguationData":[TD([[makeQuery(id+"F0.imprint","IMPRINT",EDGE,{"derivedFrom":sQuery(id+"F0.wireOp",EDGE,"a40adc37-d9a3-401c-b6fb-74b30e9c8a01")}),1.0]])]});
            var Q48;
            Q48=makeQuery(id+"F0.imprint","IMPRINT",FACE,{"disambiguationData":[TD([[makeQuery(id+"F0.imprint","IMPRINT",EDGE,{"derivedFrom":sQuery(id+"F0.wireOp",EDGE,"687f15e6-87b3-4403-92c9-e12ab6a5c124")}),1.0]])]});
            var Q49;
            Q49=makeQuery(id+"F0.imprint","IMPRINT",FACE,{"disambiguationData":[TD([[makeQuery(id+"F0.imprint","IMPRINT",EDGE,{"derivedFrom":sQuery(id+"F0.wireOp",EDGE,"7d00cad5-fac4-4050-b715-21e8bdcc284b39.MirrorCS")}),-1.0]])]});
            var Q50;
            Q50=makeQuery(id+"F0.imprint","IMPRINT",FACE,{"disambiguationData":[TD([[makeQuery(id+"F0.imprint","IMPRINT",EDGE,{"derivedFrom":sQuery(id+"F0.wireOp",EDGE,"7d00cad5-fac4-4050-b715-21e8bdcc284b46.MirrorCS")}),-1.0]])]});
            var Q51;
            {var subQ1=sQuery(id+"F0.wireOp",EDGE,"7d00cad5-fac4-4050-b715-21e8bdcc284b41.MirrorCS");Q51=makeQuery(id+"F0.imprint","IMPRINT",FACE,{"disambiguationData":[TD([[makeQuery(id+"F0.imprint","IMPRINT",EDGE,{"derivedFrom":subQ1}),-1.0]])]});}
            var Q52;
            {var subQ5=sQuery(id+"F0.wireOp",EDGE,"7d00cad5-fac4-4050-b715-21e8bdcc284b22.MirrorCS");Q52=makeQuery(id+"F0.imprint","IMPRINT",FACE,{"disambiguationData":[TD([[makeQuery(id+"F0.imprint","IMPRINT",EDGE,{"derivedFrom":subQ5}),-1.0]])]});}
            var Q53;
            {var subQ4=sQuery(id+"F0.wireOp",EDGE,"7d00cad5-fac4-4050-b715-21e8bdcc284b31.MirrorCS");Q53=makeQuery(id+"F0.imprint","IMPRINT",FACE,{"disambiguationData":[TD([[makeQuery(id+"F0.imprint","IMPRINT",EDGE,{"derivedFrom":subQ4}),-1.0]])]});}
            var Q54;
            {var subQ4=sQuery(id+"F0.wireOp",EDGE,"7d00cad5-fac4-4050-b715-21e8bdcc284b44.MirrorCS");Q54=makeQuery(id+"F0.imprint","IMPRINT",FACE,{"disambiguationData":[TD([[makeQuery(id+"F0.imprint","IMPRINT",EDGE,{"derivedFrom":subQ4}),-1.0]])]});}
            var Q55;
            {var subQ0=sQuery(id+"F0.wireOp",EDGE,"7d00cad5-fac4-4050-b715-21e8bdcc284b17.MirrorCS");Q55=makeQuery(id+"F0.imprint","IMPRINT",FACE,{"disambiguationData":[TD([[makeQuery(id+"F0.imprint","IMPRINT",EDGE,{"derivedFrom":subQ0}),-1.0]])]});}
            var Q56;
            Q56=makeQuery(id+"F0.imprint","IMPRINT",FACE,{"disambiguationData":[TD([[makeQuery(id+"F0.imprint","IMPRINT",EDGE,{"derivedFrom":sQuery(id+"F0.wireOp",EDGE,"7d00cad5-fac4-4050-b715-21e8bdcc284b28.MirrorCS")}),-1.0]])]});
            var Q57;
            {var subQ1=sQuery(id+"F0.wireOp",EDGE,"7d00cad5-fac4-4050-b715-21e8bdcc284b15.MirrorCS");Q57=makeQuery(id+"F0.imprint","IMPRINT",FACE,{"disambiguationData":[TD([[makeQuery(id+"F0.imprint","IMPRINT",EDGE,{"derivedFrom":subQ1}),-1.0]])]});}
            var Q58;
            {var subQ2=sQuery(id+"F0.wireOp",EDGE,"7d00cad5-fac4-4050-b715-21e8bdcc284b7.MirrorCS");Q58=makeQuery(id+"F0.imprint","IMPRINT",FACE,{"disambiguationData":[TD([[makeQuery(id+"F0.imprint","IMPRINT",EDGE,{"derivedFrom":subQ2}),-1.0]])]});}
            var Q59;
            {var subQ0=sQuery(id+"F0.wireOp",EDGE,"83a64bb6-06e1-48cd-aad0-cc63c7a6108e117.MirrorCS");Q59=makeQuery(id+"F0.imprint","IMPRINT",FACE,{"disambiguationData":[TD([[makeQuery(id+"F0.imprint","IMPRINT",EDGE,{"derivedFrom":subQ0}),1.0]])]});}
            var Q60;
            Q60=makeQuery(id+"F0.imprint","IMPRINT",FACE,{"disambiguationData":[TD([[makeQuery(id+"F0.imprint","IMPRINT",EDGE,{"derivedFrom":sQuery(id+"F0.wireOp",EDGE,"83a64bb6-06e1-48cd-aad0-cc63c7a6108e82.MirrorCS")}),1.0]])]});
            var Q61;
            {var subQ1=sQuery(id+"F0.wireOp",EDGE,"83a64bb6-06e1-48cd-aad0-cc63c7a6108e25.MirrorCS");Q61=makeQuery(id+"F0.imprint","IMPRINT",FACE,{"disambiguationData":[TD([[makeQuery(id+"F0.imprint","IMPRINT",EDGE,{"derivedFrom":subQ1}),1.0]])]});}
            var Q62;
            {var subQ1=sQuery(id+"F0.wireOp",EDGE,"83a64bb6-06e1-48cd-aad0-cc63c7a6108e12.MirrorCS");Q62=makeQuery(id+"F0.imprint","IMPRINT",FACE,{"disambiguationData":[TD([[makeQuery(id+"F0.imprint","IMPRINT",EDGE,{"derivedFrom":subQ1}),1.0]])]});}
            var Q63;
            Q63=makeQuery(id+"F0.imprint","IMPRINT",FACE,{"disambiguationData":[TD([[makeQuery(id+"F0.imprint","IMPRINT",EDGE,{"derivedFrom":sQuery(id+"F0.wireOp",EDGE,"83a64bb6-06e1-48cd-aad0-cc63c7a6108e37.MirrorCS")}),1.0]])]});
            var Q64;
            Q64=makeQuery(id+"F0.imprint","IMPRINT",FACE,{"disambiguationData":[TD([[makeQuery(id+"F0.imprint","IMPRINT",EDGE,{"derivedFrom":sQuery(id+"F0.wireOp",EDGE,"83a64bb6-06e1-48cd-aad0-cc63c7a6108e57.MirrorCS")}),1.0]])]});
            var Q65;
            {var subQ4=sQuery(id+"F0.wireOp",EDGE,"83a64bb6-06e1-48cd-aad0-cc63c7a6108e53.MirrorCS");Q65=makeQuery(id+"F0.imprint","IMPRINT",FACE,{"disambiguationData":[TD([[makeQuery(id+"F0.imprint","IMPRINT",EDGE,{"derivedFrom":subQ4}),1.0]])]});}
            var Q66;
            {var subQ5=sQuery(id+"F0.wireOp",EDGE,"83a64bb6-06e1-48cd-aad0-cc63c7a6108e81.MirrorCS");Q66=makeQuery(id+"F0.imprint","IMPRINT",FACE,{"disambiguationData":[TD([[makeQuery(id+"F0.imprint","IMPRINT",EDGE,{"derivedFrom":subQ5}),1.0]])]});}
            var Q67;
            Q67=makeQuery(id+"F0.imprint","IMPRINT",FACE,{"disambiguationData":[TD([[makeQuery(id+"F0.imprint","IMPRINT",EDGE,{"derivedFrom":sQuery(id+"F0.wireOp",EDGE,"83a64bb6-06e1-48cd-aad0-cc63c7a6108e115.MirrorCS")}),1.0]])]});
            var Q68;
            {var subQ1=sQuery(id+"F0.wireOp",EDGE,"83a64bb6-06e1-48cd-aad0-cc63c7a6108e83.MirrorCS");Q68=makeQuery(id+"F0.imprint","IMPRINT",FACE,{"disambiguationData":[TD([[makeQuery(id+"F0.imprint","IMPRINT",EDGE,{"derivedFrom":subQ1}),1.0]])]});}
            var Q69;
            {var subQ1=sQuery(id+"F0.wireOp",EDGE,"83a64bb6-06e1-48cd-aad0-cc63c7a6108e110.MirrorCS");Q69=makeQuery(id+"F0.imprint","IMPRINT",FACE,{"disambiguationData":[TD([[makeQuery(id+"F0.imprint","IMPRINT",EDGE,{"derivedFrom":subQ1}),-1.0]])]});}
            var Q70;
            {var subQ6=sQuery(id+"F0.wireOp",EDGE,"83a64bb6-06e1-48cd-aad0-cc63c7a6108e51.MirrorCS");Q70=makeQuery(id+"F0.imprint","IMPRINT",FACE,{"disambiguationData":[TD([[makeQuery(id+"F0.imprint","IMPRINT",EDGE,{"derivedFrom":subQ6}),-1.0]])]});}
            var Q71;
            Q71=makeQuery(id+"F0.imprint","IMPRINT",FACE,{"disambiguationData":[TD([[makeQuery(id+"F0.imprint","IMPRINT",EDGE,{"derivedFrom":sQuery(id+"F0.wireOp",EDGE,"83a64bb6-06e1-48cd-aad0-cc63c7a6108e42.MirrorCS")}),-1.0]])]});
            var Q72;
            {var subQ4=sQuery(id+"F0.wireOp",EDGE,"83a64bb6-06e1-48cd-aad0-cc63c7a6108e78.MirrorCS");Q72=makeQuery(id+"F0.imprint","IMPRINT",FACE,{"disambiguationData":[TD([[makeQuery(id+"F0.imprint","IMPRINT",EDGE,{"derivedFrom":subQ4}),-1.0]])]});}
            var Q73;
            Q73=makeQuery(id+"F0.imprint","IMPRINT",FACE,{"disambiguationData":[TD([[makeQuery(id+"F0.imprint","IMPRINT",EDGE,{"derivedFrom":sQuery(id+"F0.wireOp",EDGE,"83a64bb6-06e1-48cd-aad0-cc63c7a6108e50.MirrorCS")}),-1.0]])]});
            var Q74;
            {var subQ1=sQuery(id+"F0.wireOp",EDGE,"83a64bb6-06e1-48cd-aad0-cc63c7a6108e85.MirrorCS");Q74=makeQuery(id+"F0.imprint","IMPRINT",FACE,{"disambiguationData":[TD([[makeQuery(id+"F0.imprint","IMPRINT",EDGE,{"derivedFrom":subQ1}),-1.0]])]});}
            var Q75;
            {var subQ0=sQuery(id+"F0.wireOp",EDGE,"83a64bb6-06e1-48cd-aad0-cc63c7a6108e33.MirrorCS");Q75=makeQuery(id+"F0.imprint","IMPRINT",FACE,{"disambiguationData":[TD([[makeQuery(id+"F0.imprint","IMPRINT",EDGE,{"derivedFrom":subQ0}),-1.0]])]});}
            var Q76;
            {var subQ4=sQuery(id+"F0.wireOp",EDGE,"83a64bb6-06e1-48cd-aad0-cc63c7a6108e94.MirrorCS");Q76=makeQuery(id+"F0.imprint","IMPRINT",FACE,{"disambiguationData":[TD([[makeQuery(id+"F0.imprint","IMPRINT",EDGE,{"derivedFrom":subQ4}),-1.0]])]});}
            var Q77;
            {var subQ6=sQuery(id+"F0.wireOp",EDGE,"83a64bb6-06e1-48cd-aad0-cc63c7a6108e10.MirrorCS");Q77=makeQuery(id+"F0.imprint","IMPRINT",FACE,{"disambiguationData":[TD([[makeQuery(id+"F0.imprint","IMPRINT",EDGE,{"derivedFrom":subQ6}),-1.0]])]});}
            var Q78;
            {var subQ0=sQuery(id+"F0.wireOp",EDGE,"83a64bb6-06e1-48cd-aad0-cc63c7a6108e52.MirrorCS");Q78=makeQuery(id+"F0.imprint","IMPRINT",FACE,{"disambiguationData":[TD([[makeQuery(id+"F0.imprint","IMPRINT",EDGE,{"derivedFrom":subQ0}),-1.0]])]});}
            var Q79;
            Q79=makeQuery(id+"F0.imprint","IMPRINT",FACE,{"disambiguationData":[TD([[makeQuery(id+"F0.imprint","IMPRINT",EDGE,{"derivedFrom":sQuery(id+"F0.wireOp",EDGE,"E1")}),-1.0]])]});
            var Q80;
            Q80=makeQuery(id+"F0.imprint","IMPRINT",FACE,{"disambiguationData":[TD([[makeQuery(id+"F0.imprint","IMPRINT",EDGE,{"derivedFrom":sQuery(id+"F0.wireOp",EDGE,"83a64bb6-06e1-48cd-aad0-cc63c7a6108e27.MirrorCS")}),1.0]])]});
            extrude(context, id + "F1", {"entities" : qUnion([Q0, Q1, Q2, Q3, Q4, Q5, Q6, Q7, Q8, Q9, Q10, Q11, Q12, Q13, Q14, Q15, Q16, Q17, Q18, Q19, Q20, Q21, Q22, Q23, Q24, Q25, Q26, Q27, Q28, Q29, Q30, Q31, Q32, Q33, Q34, Q35, Q36, Q37, Q38, Q39, Q40, Q41, Q42, Q43, Q44, Q45, Q46, Q47, Q48, Q49, Q50, Q51, Q52, Q53, Q54, Q55, Q56, Q57, Q58, Q59, Q60, Q61, Q62, Q63, Q64, Q65, Q66, Q67, Q68, Q69, Q70, Q71, Q72, Q73, Q74, Q75, Q76, Q77, Q78, Q79, Q80]), "depth" : 12.7 * mm});
        }
        {
            var Q0;
            Q0=qCreatedBy(makeId("Front.planeOp"),FACE);
            var sketch = newSketch(context, id + "F2", { "sketchPlane" : qUnion([Q0])});
            skCircle(sketch, "E572", {"center": v(23.04, -32.45) * mm, "radius": 19.05 * mm});
            skCircle(sketch, "E573", {"center": v(23.04, -32.45) * mm, "radius": 6.35 * mm});
            skLineSegment(sketch, "E574", {"start": v(23.04, -13.4) * mm, "end": v(23.04, -51.5) * mm, "construction": true});
            skLineSegment(sketch, "E575", {"start": v(4, -32.45) * mm, "end": v(42.1, -32.45) * mm, "construction": true});
            skLineSegment(sketch, "E576", {"start": v(41.13, -28.9) * mm, "end": v(41.3, -30.83) * mm});
            skLineSegment(sketch, "E577", {"start": v(44.41, -28.59) * mm, "end": v(41.68, -28.35) * mm});
            skLineSegment(sketch, "E578", {"start": v(41.94, -31.28) * mm, "end": v(44.59, -30.57) * mm});
            skLineSegment(sketch, "E579", {"start": v(44.88, -29.05) * mm, "end": v(44.96, -30.03) * mm});
            skPoint(sketch, "E580.visualSharp", {"position": v(44.84, -28.63) * mm});
            skArc(sketch, "E580.filletArc", {"start": v(44.88, -29.05) * mm, "mid": v(44.73, -28.74) * mm, "end": v(44.41, -28.59) * mm});
            skPoint(sketch, "E581.visualSharp", {"position": v(41.08, -28.3) * mm});
            skArc(sketch, "E581.filletArc", {"start": v(41.68, -28.35) * mm, "mid": v(41.28, -28.5) * mm, "end": v(41.13, -28.9) * mm});
            skPoint(sketch, "E582.visualSharp", {"position": v(41.35, -31.43) * mm});
            skArc(sketch, "E582.filletArc", {"start": v(41.3, -30.83) * mm, "mid": v(41.52, -31.2) * mm, "end": v(41.94, -31.28) * mm});
            skPoint(sketch, "E583.visualSharp", {"position": v(45, -30.46) * mm});
            skArc(sketch, "E583.filletArc", {"start": v(44.59, -30.57) * mm, "mid": v(44.87, -30.37) * mm, "end": v(44.96, -30.03) * mm});
            skLineSegment(sketch, "E584.0", {"start": v(45, -30.46) * mm, "end": v(44.84, -28.63) * mm, "construction": true});
            skLineSegment(sketch, "E585", {"start": v(38.78, -23.42) * mm, "end": v(39.73, -25.1) * mm});
            skLineSegment(sketch, "E586", {"start": v(41.64, -21.78) * mm, "end": v(39.05, -22.69) * mm});
            skLineSegment(sketch, "E587", {"start": v(40.5, -25.25) * mm, "end": v(42.61, -23.51) * mm});
            skLineSegment(sketch, "E588", {"start": v(42.25, -22.01) * mm, "end": v(42.73, -22.87) * mm});
            skPoint(sketch, "E589.visualSharp", {"position": v(42.04, -21.64) * mm});
            skArc(sketch, "E589.filletArc", {"start": v(42.25, -22.01) * mm, "mid": v(41.99, -21.78) * mm, "end": v(41.64, -21.78) * mm});
            skPoint(sketch, "E590.visualSharp", {"position": v(38.48, -22.89) * mm});
            skArc(sketch, "E590.filletArc", {"start": v(39.05, -22.69) * mm, "mid": v(38.75, -22.99) * mm, "end": v(38.78, -23.42) * mm});
            skPoint(sketch, "E591.visualSharp", {"position": v(40.02, -25.63) * mm});
            skArc(sketch, "E591.filletArc", {"start": v(39.73, -25.1) * mm, "mid": v(40.08, -25.36) * mm, "end": v(40.5, -25.25) * mm});
            skPoint(sketch, "E592.visualSharp", {"position": v(42.94, -23.24) * mm});
            skArc(sketch, "E592.filletArc", {"start": v(42.61, -23.51) * mm, "mid": v(42.8, -23.21) * mm, "end": v(42.73, -22.87) * mm});
            skLineSegment(sketch, "E593.0", {"start": v(42.94, -23.24) * mm, "end": v(42.04, -21.64) * mm, "construction": true});
            skLineSegment(sketch, "E594", {"start": v(35.02, -18.63) * mm, "end": v(36.4, -20) * mm});
            skLineSegment(sketch, "E595", {"start": v(37.34, -16.28) * mm, "end": v(35.1, -17.86) * mm});
            skLineSegment(sketch, "E596", {"start": v(37.17, -19.94) * mm, "end": v(38.74, -17.69) * mm});
            skLineSegment(sketch, "E597", {"start": v(37.99, -16.34) * mm, "end": v(38.69, -17.04) * mm});
            skPoint(sketch, "E598.visualSharp", {"position": v(37.69, -16.04) * mm});
            skArc(sketch, "E598.filletArc", {"start": v(37.99, -16.34) * mm, "mid": v(37.67, -16.2) * mm, "end": v(37.34, -16.28) * mm});
            skPoint(sketch, "E599.visualSharp", {"position": v(34.6, -18.2) * mm});
            skArc(sketch, "E599.filletArc", {"start": v(35.1, -17.86) * mm, "mid": v(34.88, -18.23) * mm, "end": v(35.02, -18.63) * mm});
            skPoint(sketch, "E600.visualSharp", {"position": v(36.82, -20.43) * mm});
            skArc(sketch, "E600.filletArc", {"start": v(36.4, -20) * mm, "mid": v(36.8, -20.15) * mm, "end": v(37.17, -19.94) * mm});
            skPoint(sketch, "E601.visualSharp", {"position": v(38.99, -17.34) * mm});
            skArc(sketch, "E601.filletArc", {"start": v(38.74, -17.69) * mm, "mid": v(38.83, -17.35) * mm, "end": v(38.69, -17.04) * mm});
            skLineSegment(sketch, "E602.0", {"start": v(38.99, -17.34) * mm, "end": v(37.69, -16.04) * mm, "construction": true});
            skLineSegment(sketch, "E603", {"start": v(30.44, -15.62) * mm, "end": v(32.12, -16.6) * mm});
            skLineSegment(sketch, "E604", {"start": v(32.07, -12.76) * mm, "end": v(30.3, -14.86) * mm});
            skLineSegment(sketch, "E605", {"start": v(32.85, -16.33) * mm, "end": v(33.79, -13.75) * mm});
            skLineSegment(sketch, "E606", {"start": v(32.71, -12.64) * mm, "end": v(33.57, -13.14) * mm});
            skPoint(sketch, "E607.visualSharp", {"position": v(32.34, -12.43) * mm});
            skArc(sketch, "E607.filletArc", {"start": v(32.71, -12.64) * mm, "mid": v(32.37, -12.58) * mm, "end": v(32.07, -12.76) * mm});
            skPoint(sketch, "E608.visualSharp", {"position": v(29.92, -15.32) * mm});
            skArc(sketch, "E608.filletArc", {"start": v(30.3, -14.86) * mm, "mid": v(30.2, -15.27) * mm, "end": v(30.44, -15.62) * mm});
            skPoint(sketch, "E609.visualSharp", {"position": v(32.65, -16.9) * mm});
            skArc(sketch, "E609.filletArc", {"start": v(32.12, -16.6) * mm, "mid": v(32.55, -16.63) * mm, "end": v(32.85, -16.33) * mm});
            skPoint(sketch, "E610.visualSharp", {"position": v(33.94, -13.35) * mm});
            skArc(sketch, "E610.filletArc", {"start": v(33.79, -13.75) * mm, "mid": v(33.79, -13.4) * mm, "end": v(33.57, -13.14) * mm});
            skLineSegment(sketch, "E611.0", {"start": v(33.94, -13.35) * mm, "end": v(32.34, -12.43) * mm, "construction": true});
            skLineSegment(sketch, "E612", {"start": v(24.93, -14.08) * mm, "end": v(26.84, -14.42) * mm});
            skLineSegment(sketch, "E613", {"start": v(25.47, -10.83) * mm, "end": v(24.54, -13.41) * mm});
            skLineSegment(sketch, "E614", {"start": v(27.43, -13.92) * mm, "end": v(27.43, -11.18) * mm});
            skLineSegment(sketch, "E615", {"start": v(26.04, -10.5) * mm, "end": v(27.01, -10.68) * mm});
            skPoint(sketch, "E616.visualSharp", {"position": v(25.62, -10.43) * mm});
            skArc(sketch, "E616.filletArc", {"start": v(26.04, -10.5) * mm, "mid": v(25.7, -10.57) * mm, "end": v(25.47, -10.83) * mm});
            skPoint(sketch, "E617.visualSharp", {"position": v(24.33, -13.98) * mm});
            skArc(sketch, "E617.filletArc", {"start": v(24.54, -13.41) * mm, "mid": v(24.57, -13.84) * mm, "end": v(24.93, -14.08) * mm});
            skPoint(sketch, "E618.visualSharp", {"position": v(27.43, -14.53) * mm});
            skArc(sketch, "E618.filletArc", {"start": v(26.84, -14.42) * mm, "mid": v(27.25, -14.31) * mm, "end": v(27.43, -13.92) * mm});
            skPoint(sketch, "E619.visualSharp", {"position": v(27.43, -10.75) * mm});
            skArc(sketch, "E619.filletArc", {"start": v(27.43, -11.18) * mm, "mid": v(27.31, -10.85) * mm, "end": v(27.01, -10.68) * mm});
            skLineSegment(sketch, "E620.0", {"start": v(27.43, -10.75) * mm, "end": v(25.62, -10.43) * mm, "construction": true});
            skLineSegment(sketch, "E621.MirrorCS", {"start": v(20.05, -10.5) * mm, "end": v(19.08, -10.68) * mm});
            skArc(sketch, "E622.MirrorCS", {"start": v(20.05, -10.5) * mm, "mid": v(20.4, -10.57) * mm, "end": v(20.61, -10.83) * mm});
            skLineSegment(sketch, "E623.MirrorCS", {"start": v(1.09, -30.46) * mm, "end": v(1.25, -28.63) * mm, "construction": true});
            skArc(sketch, "E624.MirrorCS", {"start": v(18.66, -11.18) * mm, "mid": v(18.78, -10.85) * mm, "end": v(19.08, -10.68) * mm});
            skLineSegment(sketch, "E625.MirrorCS", {"start": v(1.21, -29.05) * mm, "end": v(1.13, -30.03) * mm});
            skArc(sketch, "E626.MirrorCS", {"start": v(13.38, -12.64) * mm, "mid": v(13.72, -12.58) * mm, "end": v(14.02, -12.76) * mm});
            skArc(sketch, "E627.MirrorCS", {"start": v(11, -17.86) * mm, "mid": v(11.21, -18.23) * mm, "end": v(11.06, -18.63) * mm});
            skArc(sketch, "E628.MirrorCS", {"start": v(6.36, -25.1) * mm, "mid": v(6.01, -25.36) * mm, "end": v(5.6, -25.25) * mm});
            skArc(sketch, "E629.MirrorCS", {"start": v(8.1, -16.34) * mm, "mid": v(8.41, -16.2) * mm, "end": v(8.75, -16.28) * mm});
            skLineSegment(sketch, "E630.MirrorCS", {"start": v(13.38, -12.64) * mm, "end": v(12.52, -13.14) * mm});
            skArc(sketch, "E631.MirrorCS", {"start": v(7.35, -17.69) * mm, "mid": v(7.26, -17.35) * mm, "end": v(7.4, -17.04) * mm});
            skArc(sketch, "E632.MirrorCS", {"start": v(3.48, -23.51) * mm, "mid": v(3.3, -23.21) * mm, "end": v(3.35, -22.87) * mm});
            skArc(sketch, "E633.MirrorCS", {"start": v(13.97, -16.6) * mm, "mid": v(13.54, -16.63) * mm, "end": v(13.24, -16.33) * mm});
            skArc(sketch, "E634.MirrorCS", {"start": v(15.78, -14.86) * mm, "mid": v(15.9, -15.27) * mm, "end": v(15.65, -15.62) * mm});
            skArc(sketch, "E635.MirrorCS", {"start": v(9.7, -20) * mm, "mid": v(9.29, -20.15) * mm, "end": v(8.92, -19.94) * mm});
            skArc(sketch, "E636.MirrorCS", {"start": v(7.04, -22.69) * mm, "mid": v(7.34, -22.99) * mm, "end": v(7.31, -23.42) * mm});
            skLineSegment(sketch, "E637.MirrorCS", {"start": v(8.1, -16.34) * mm, "end": v(7.4, -17.04) * mm});
            skArc(sketch, "E638.MirrorCS", {"start": v(1.5, -30.57) * mm, "mid": v(1.22, -30.37) * mm, "end": v(1.13, -30.03) * mm});
            skLineSegment(sketch, "E639.MirrorCS", {"start": v(7.1, -17.34) * mm, "end": v(8.4, -16.04) * mm, "construction": true});
            skLineSegment(sketch, "E640.MirrorCS", {"start": v(18.66, -10.75) * mm, "end": v(20.47, -10.43) * mm, "construction": true});
            skArc(sketch, "E641.MirrorCS", {"start": v(3.84, -22.01) * mm, "mid": v(4.1, -21.78) * mm, "end": v(4.45, -21.78) * mm});
            skArc(sketch, "E642.MirrorCS", {"start": v(12.3, -13.75) * mm, "mid": v(12.3, -13.4) * mm, "end": v(12.52, -13.14) * mm});
            skArc(sketch, "E643.MirrorCS", {"start": v(21.55, -13.41) * mm, "mid": v(21.51, -13.84) * mm, "end": v(21.16, -14.08) * mm});
            skLineSegment(sketch, "E644.MirrorCS", {"start": v(3.84, -22.01) * mm, "end": v(3.35, -22.87) * mm});
            skArc(sketch, "E645.MirrorCS", {"start": v(4.79, -30.83) * mm, "mid": v(4.57, -31.2) * mm, "end": v(4.15, -31.28) * mm});
            skLineSegment(sketch, "E646.MirrorCS", {"start": v(3.15, -23.24) * mm, "end": v(4.05, -21.64) * mm, "construction": true});
            skLineSegment(sketch, "E647.MirrorCS", {"start": v(12.15, -13.35) * mm, "end": v(13.75, -12.43) * mm, "construction": true});
            skArc(sketch, "E648.MirrorCS", {"start": v(19.25, -14.42) * mm, "mid": v(18.84, -14.31) * mm, "end": v(18.66, -13.92) * mm});
            skArc(sketch, "E649.MirrorCS", {"start": v(1.21, -29.05) * mm, "mid": v(1.36, -28.74) * mm, "end": v(1.67, -28.59) * mm});
            skArc(sketch, "E650.MirrorCS", {"start": v(4.4, -28.35) * mm, "mid": v(4.8, -28.5) * mm, "end": v(4.96, -28.9) * mm});
            skPoint(sketch, "E651.MirrorP", {"position": v(4.73, -31.43) * mm});
            skPoint(sketch, "E652.MirrorP", {"position": v(9.27, -20.43) * mm});
            skPoint(sketch, "E653.MirrorP", {"position": v(13.44, -16.9) * mm});
            skPoint(sketch, "E654.MirrorP", {"position": v(21.76, -13.98) * mm});
            skPoint(sketch, "E655.MirrorP", {"position": v(7.6, -22.89) * mm});
            skPoint(sketch, "E656.MirrorP", {"position": v(3.15, -23.24) * mm});
            skPoint(sketch, "E657.MirrorP", {"position": v(18.66, -10.75) * mm});
            skLineSegment(sketch, "E658.MirrorCS", {"start": v(15.65, -15.62) * mm, "end": v(13.97, -16.6) * mm});
            skLineSegment(sketch, "E659.MirrorCS", {"start": v(18.66, -13.92) * mm, "end": v(18.66, -11.18) * mm});
            skLineSegment(sketch, "E660.MirrorCS", {"start": v(13.24, -16.33) * mm, "end": v(12.3, -13.75) * mm});
            skLineSegment(sketch, "E661.MirrorCS", {"start": v(8.75, -16.28) * mm, "end": v(11, -17.86) * mm});
            skLineSegment(sketch, "E662.MirrorCS", {"start": v(14.02, -12.76) * mm, "end": v(15.78, -14.86) * mm});
            skLineSegment(sketch, "E663.MirrorCS", {"start": v(5.6, -25.25) * mm, "end": v(3.48, -23.51) * mm});
            skLineSegment(sketch, "E664.MirrorCS", {"start": v(8.92, -19.94) * mm, "end": v(7.35, -17.69) * mm});
            skPoint(sketch, "E665.MirrorP", {"position": v(1.09, -30.46) * mm});
            skPoint(sketch, "E666.MirrorP", {"position": v(7.1, -17.34) * mm});
            skLineSegment(sketch, "E667.MirrorCS", {"start": v(4.45, -21.78) * mm, "end": v(7.04, -22.69) * mm});
            skPoint(sketch, "E668.MirrorP", {"position": v(12.15, -13.35) * mm});
            skPoint(sketch, "E669.MirrorP", {"position": v(20.47, -10.43) * mm});
            skLineSegment(sketch, "E670.MirrorCS", {"start": v(7.31, -23.42) * mm, "end": v(6.36, -25.1) * mm});
            skLineSegment(sketch, "E671.MirrorCS", {"start": v(1.67, -28.59) * mm, "end": v(4.4, -28.35) * mm});
            skLineSegment(sketch, "E672.MirrorCS", {"start": v(4.96, -28.9) * mm, "end": v(4.79, -30.83) * mm});
            skLineSegment(sketch, "E673.MirrorCS", {"start": v(4.15, -31.28) * mm, "end": v(1.5, -30.57) * mm});
            skPoint(sketch, "E674.MirrorP", {"position": v(18.66, -14.53) * mm});
            skPoint(sketch, "E675.MirrorP", {"position": v(4.05, -21.64) * mm});
            skLineSegment(sketch, "E676.MirrorCS", {"start": v(11.06, -18.63) * mm, "end": v(9.7, -20) * mm});
            skPoint(sketch, "E677.MirrorP", {"position": v(6.06, -25.63) * mm});
            skPoint(sketch, "E678.MirrorP", {"position": v(13.75, -12.43) * mm});
            skLineSegment(sketch, "E679.MirrorCS", {"start": v(21.16, -14.08) * mm, "end": v(19.25, -14.42) * mm});
            skLineSegment(sketch, "E680.MirrorCS", {"start": v(20.61, -10.83) * mm, "end": v(21.55, -13.41) * mm});
            skPoint(sketch, "E681.MirrorP", {"position": v(5, -28.3) * mm});
            skPoint(sketch, "E682.MirrorP", {"position": v(11.5, -18.2) * mm});
            skPoint(sketch, "E683.MirrorP", {"position": v(16.17, -15.32) * mm});
            skPoint(sketch, "E684.MirrorP", {"position": v(1.25, -28.63) * mm});
            skPoint(sketch, "E685.MirrorP", {"position": v(8.4, -16.04) * mm});
            skLineSegment(sketch, "E686.MirrorCS", {"start": v(42.25, -42.88) * mm, "end": v(42.73, -42.02) * mm});
            skArc(sketch, "E687.MirrorCS", {"start": v(37.99, -48.55) * mm, "mid": v(37.67, -48.7) * mm, "end": v(37.34, -48.6) * mm});
            skLineSegment(sketch, "E688.MirrorCS", {"start": v(32.71, -52.25) * mm, "end": v(33.57, -51.76) * mm});
            skArc(sketch, "E689.MirrorCS", {"start": v(20.05, -54.39) * mm, "mid": v(20.4, -54.32) * mm, "end": v(20.61, -54.06) * mm});
            skArc(sketch, "E690.MirrorCS", {"start": v(1.5, -34.32) * mm, "mid": v(1.22, -34.52) * mm, "end": v(1.13, -34.86) * mm});
            skLineSegment(sketch, "E691.MirrorCS", {"start": v(37.99, -48.55) * mm, "end": v(38.69, -47.85) * mm});
            skLineSegment(sketch, "E692.MirrorCS", {"start": v(8.1, -48.55) * mm, "end": v(7.4, -47.85) * mm});
            skArc(sketch, "E693.MirrorCS", {"start": v(44.59, -34.32) * mm, "mid": v(44.87, -34.52) * mm, "end": v(44.96, -34.86) * mm});
            skArc(sketch, "E694.MirrorCS", {"start": v(41.3, -34.06) * mm, "mid": v(41.52, -33.69) * mm, "end": v(41.94, -33.61) * mm});
            skArc(sketch, "E695.MirrorCS", {"start": v(41.68, -36.54) * mm, "mid": v(41.28, -36.4) * mm, "end": v(41.13, -36) * mm});
            skArc(sketch, "E696.MirrorCS", {"start": v(44.88, -35.84) * mm, "mid": v(44.73, -36.16) * mm, "end": v(44.41, -36.3) * mm});
            skLineSegment(sketch, "E697.MirrorCS", {"start": v(44.88, -35.84) * mm, "end": v(44.96, -34.86) * mm});
            skArc(sketch, "E698.MirrorCS", {"start": v(7.04, -42.2) * mm, "mid": v(7.34, -41.9) * mm, "end": v(7.31, -41.48) * mm});
            skArc(sketch, "E699.MirrorCS", {"start": v(27.43, -53.71) * mm, "mid": v(27.31, -54.04) * mm, "end": v(27.01, -54.21) * mm});
            skArc(sketch, "E700.MirrorCS", {"start": v(9.7, -44.89) * mm, "mid": v(9.29, -44.74) * mm, "end": v(8.92, -44.96) * mm});
            skArc(sketch, "E701.MirrorCS", {"start": v(26.84, -50.47) * mm, "mid": v(27.25, -50.58) * mm, "end": v(27.43, -50.97) * mm});
            skArc(sketch, "E702.MirrorCS", {"start": v(15.78, -50.03) * mm, "mid": v(15.9, -49.62) * mm, "end": v(15.65, -49.27) * mm});
            skArc(sketch, "E703.MirrorCS", {"start": v(4.4, -36.54) * mm, "mid": v(4.8, -36.4) * mm, "end": v(4.96, -36) * mm});
            skArc(sketch, "E704.MirrorCS", {"start": v(24.54, -51.48) * mm, "mid": v(24.57, -51.05) * mm, "end": v(24.93, -50.8) * mm});
            skArc(sketch, "E705.MirrorCS", {"start": v(13.97, -48.3) * mm, "mid": v(13.54, -48.26) * mm, "end": v(13.24, -48.57) * mm});
            skArc(sketch, "E706.MirrorCS", {"start": v(1.21, -35.84) * mm, "mid": v(1.36, -36.16) * mm, "end": v(1.67, -36.3) * mm});
            skLineSegment(sketch, "E707.MirrorCS", {"start": v(42.94, -41.65) * mm, "end": v(42.04, -43.25) * mm, "construction": true});
            skLineSegment(sketch, "E708.MirrorCS", {"start": v(7.1, -47.55) * mm, "end": v(8.4, -48.85) * mm, "construction": true});
            skArc(sketch, "E709.MirrorCS", {"start": v(32.71, -52.25) * mm, "mid": v(32.37, -52.3) * mm, "end": v(32.07, -52.13) * mm});
            skArc(sketch, "E710.MirrorCS", {"start": v(35.1, -47.04) * mm, "mid": v(34.88, -46.66) * mm, "end": v(35.02, -46.26) * mm});
            skArc(sketch, "E711.MirrorCS", {"start": v(38.74, -47.2) * mm, "mid": v(38.83, -47.54) * mm, "end": v(38.69, -47.85) * mm});
            skArc(sketch, "E712.MirrorCS", {"start": v(3.84, -42.88) * mm, "mid": v(4.1, -43.1) * mm, "end": v(4.45, -43.11) * mm});
            skArc(sketch, "E713.MirrorCS", {"start": v(32.12, -48.3) * mm, "mid": v(32.55, -48.26) * mm, "end": v(32.85, -48.57) * mm});
            skArc(sketch, "E714.MirrorCS", {"start": v(42.25, -42.88) * mm, "mid": v(41.99, -43.1) * mm, "end": v(41.64, -43.11) * mm});
            skArc(sketch, "E715.MirrorCS", {"start": v(8.1, -48.55) * mm, "mid": v(8.41, -48.7) * mm, "end": v(8.75, -48.6) * mm});
            skArc(sketch, "E716.MirrorCS", {"start": v(26.04, -54.39) * mm, "mid": v(25.7, -54.32) * mm, "end": v(25.47, -54.06) * mm});
            skArc(sketch, "E717.MirrorCS", {"start": v(3.48, -41.38) * mm, "mid": v(3.3, -41.68) * mm, "end": v(3.35, -42.02) * mm});
            skArc(sketch, "E718.MirrorCS", {"start": v(42.61, -41.38) * mm, "mid": v(42.8, -41.68) * mm, "end": v(42.73, -42.02) * mm});
            skArc(sketch, "E719.MirrorCS", {"start": v(4.79, -34.06) * mm, "mid": v(4.57, -33.69) * mm, "end": v(4.15, -33.61) * mm});
            skArc(sketch, "E720.MirrorCS", {"start": v(39.05, -42.2) * mm, "mid": v(38.75, -41.9) * mm, "end": v(38.78, -41.48) * mm});
            skArc(sketch, "E721.MirrorCS", {"start": v(39.73, -39.79) * mm, "mid": v(40.08, -39.54) * mm, "end": v(40.5, -39.64) * mm});
            skLineSegment(sketch, "E722.MirrorCS", {"start": v(12.15, -51.54) * mm, "end": v(13.75, -52.46) * mm, "construction": true});
            skArc(sketch, "E723.MirrorCS", {"start": v(7.35, -47.2) * mm, "mid": v(7.26, -47.54) * mm, "end": v(7.4, -47.85) * mm});
            skLineSegment(sketch, "E724.MirrorCS", {"start": v(3.15, -41.65) * mm, "end": v(4.05, -43.25) * mm, "construction": true});
            skLineSegment(sketch, "E725.MirrorCS", {"start": v(13.38, -52.25) * mm, "end": v(12.52, -51.76) * mm});
            skArc(sketch, "E726.MirrorCS", {"start": v(13.38, -52.25) * mm, "mid": v(13.72, -52.3) * mm, "end": v(14.02, -52.13) * mm});
            skArc(sketch, "E727.MirrorCS", {"start": v(12.3, -51.14) * mm, "mid": v(12.3, -51.49) * mm, "end": v(12.52, -51.76) * mm});
            skArc(sketch, "E728.MirrorCS", {"start": v(6.36, -39.79) * mm, "mid": v(6.01, -39.54) * mm, "end": v(5.6, -39.64) * mm});
            skArc(sketch, "E729.MirrorCS", {"start": v(33.79, -51.14) * mm, "mid": v(33.79, -51.49) * mm, "end": v(33.57, -51.76) * mm});
            skArc(sketch, "E730.MirrorCS", {"start": v(18.66, -53.71) * mm, "mid": v(18.78, -54.04) * mm, "end": v(19.08, -54.21) * mm});
            skArc(sketch, "E731.MirrorCS", {"start": v(21.55, -51.48) * mm, "mid": v(21.51, -51.05) * mm, "end": v(21.16, -50.8) * mm});
            skLineSegment(sketch, "E732.MirrorCS", {"start": v(26.04, -54.39) * mm, "end": v(27.01, -54.21) * mm});
            skArc(sketch, "E733.MirrorCS", {"start": v(36.4, -44.89) * mm, "mid": v(36.8, -44.74) * mm, "end": v(37.17, -44.96) * mm});
            skLineSegment(sketch, "E734.MirrorCS", {"start": v(3.84, -42.88) * mm, "end": v(3.35, -42.02) * mm});
            skArc(sketch, "E735.MirrorCS", {"start": v(30.3, -50.03) * mm, "mid": v(30.2, -49.62) * mm, "end": v(30.44, -49.27) * mm});
            skLineSegment(sketch, "E736.MirrorCS", {"start": v(38.99, -47.55) * mm, "end": v(37.69, -48.85) * mm, "construction": true});
            skArc(sketch, "E737.MirrorCS", {"start": v(11, -47.04) * mm, "mid": v(11.21, -46.66) * mm, "end": v(11.06, -46.26) * mm});
            skLineSegment(sketch, "E738.MirrorCS", {"start": v(33.94, -51.54) * mm, "end": v(32.34, -52.46) * mm, "construction": true});
            skLineSegment(sketch, "E739.MirrorCS", {"start": v(45, -34.43) * mm, "end": v(44.84, -36.27) * mm, "construction": true});
            skLineSegment(sketch, "E740.MirrorCS", {"start": v(20.05, -54.39) * mm, "end": v(19.08, -54.21) * mm});
            skLineSegment(sketch, "E741.MirrorCS", {"start": v(27.43, -54.14) * mm, "end": v(25.62, -54.46) * mm, "construction": true});
            skLineSegment(sketch, "E742.MirrorCS", {"start": v(1.21, -35.84) * mm, "end": v(1.13, -34.86) * mm});
            skArc(sketch, "E743.MirrorCS", {"start": v(19.25, -50.47) * mm, "mid": v(18.84, -50.58) * mm, "end": v(18.66, -50.97) * mm});
            skPoint(sketch, "E744.MirrorP", {"position": v(44.84, -36.27) * mm});
            skPoint(sketch, "E745.MirrorP", {"position": v(37.69, -48.85) * mm});
            skPoint(sketch, "E746.MirrorP", {"position": v(32.34, -52.46) * mm});
            skLineSegment(sketch, "E747.MirrorCS", {"start": v(8.75, -48.6) * mm, "end": v(11, -47.04) * mm});
            skPoint(sketch, "E748.MirrorP", {"position": v(4.05, -43.25) * mm});
            skLineSegment(sketch, "E749.MirrorCS", {"start": v(13.24, -48.57) * mm, "end": v(12.3, -51.14) * mm});
            skLineSegment(sketch, "E750.MirrorCS", {"start": v(32.85, -48.57) * mm, "end": v(33.79, -51.14) * mm});
            skPoint(sketch, "E751.MirrorP", {"position": v(18.66, -50.37) * mm});
            skLineSegment(sketch, "E752.MirrorCS", {"start": v(41.94, -33.61) * mm, "end": v(44.59, -34.32) * mm});
            skLineSegment(sketch, "E753.MirrorCS", {"start": v(44.41, -36.3) * mm, "end": v(41.68, -36.54) * mm});
            skLineSegment(sketch, "E754.MirrorCS", {"start": v(41.13, -36) * mm, "end": v(41.3, -34.06) * mm});
            skLineSegment(sketch, "E755.MirrorCS", {"start": v(40.5, -39.64) * mm, "end": v(42.61, -41.38) * mm});
            skLineSegment(sketch, "E756.MirrorCS", {"start": v(41.64, -43.11) * mm, "end": v(39.05, -42.2) * mm});
            skLineSegment(sketch, "E757.MirrorCS", {"start": v(38.78, -41.48) * mm, "end": v(39.73, -39.79) * mm});
            skLineSegment(sketch, "E758.MirrorCS", {"start": v(18.66, -50.97) * mm, "end": v(18.66, -53.71) * mm});
            skLineSegment(sketch, "E759.MirrorCS", {"start": v(37.17, -44.96) * mm, "end": v(38.74, -47.2) * mm});
            skLineSegment(sketch, "E760.MirrorCS", {"start": v(32.07, -52.13) * mm, "end": v(30.3, -50.03) * mm});
            skPoint(sketch, "E761.MirrorP", {"position": v(20.47, -54.46) * mm});
            skPoint(sketch, "E762.MirrorP", {"position": v(42.94, -41.65) * mm});
            skPoint(sketch, "E763.MirrorP", {"position": v(27.43, -54.14) * mm});
            skLineSegment(sketch, "E764.MirrorCS", {"start": v(15.65, -49.27) * mm, "end": v(13.97, -48.3) * mm});
            skLineSegment(sketch, "E765.MirrorCS", {"start": v(37.34, -48.6) * mm, "end": v(35.1, -47.04) * mm});
            skLineSegment(sketch, "E766.MirrorCS", {"start": v(30.44, -49.27) * mm, "end": v(32.12, -48.3) * mm});
            skPoint(sketch, "E767.MirrorP", {"position": v(12.15, -51.54) * mm});
            skLineSegment(sketch, "E768.MirrorCS", {"start": v(35.02, -46.26) * mm, "end": v(36.4, -44.89) * mm});
            skPoint(sketch, "E769.MirrorP", {"position": v(27.43, -50.37) * mm});
            skPoint(sketch, "E770.MirrorP", {"position": v(7.1, -47.55) * mm});
            skPoint(sketch, "E771.MirrorP", {"position": v(40.02, -39.26) * mm});
            skLineSegment(sketch, "E772.MirrorCS", {"start": v(20.61, -54.06) * mm, "end": v(21.55, -51.48) * mm});
            skPoint(sketch, "E773.MirrorP", {"position": v(1.09, -34.43) * mm});
            skLineSegment(sketch, "E774.MirrorCS", {"start": v(1.09, -34.43) * mm, "end": v(1.25, -36.27) * mm, "construction": true});
            skLineSegment(sketch, "E775.MirrorCS", {"start": v(14.02, -52.13) * mm, "end": v(15.78, -50.03) * mm});
            skPoint(sketch, "E776.MirrorP", {"position": v(13.75, -52.46) * mm});
            skPoint(sketch, "E777.MirrorP", {"position": v(21.76, -50.91) * mm});
            skLineSegment(sketch, "E778.MirrorCS", {"start": v(8.92, -44.96) * mm, "end": v(7.35, -47.2) * mm});
            skPoint(sketch, "E779.MirrorP", {"position": v(1.25, -36.27) * mm});
            skPoint(sketch, "E780.MirrorP", {"position": v(16.17, -49.57) * mm});
            skLineSegment(sketch, "E781.MirrorCS", {"start": v(21.16, -50.8) * mm, "end": v(19.25, -50.47) * mm});
            skPoint(sketch, "E782.MirrorP", {"position": v(38.99, -47.55) * mm});
            skPoint(sketch, "E783.MirrorP", {"position": v(33.94, -51.54) * mm});
            skPoint(sketch, "E784.MirrorP", {"position": v(13.44, -48) * mm});
            skPoint(sketch, "E785.MirrorP", {"position": v(24.33, -50.91) * mm});
            skPoint(sketch, "E786.MirrorP", {"position": v(18.66, -54.14) * mm});
            skLineSegment(sketch, "E787.MirrorCS", {"start": v(4.96, -36) * mm, "end": v(4.79, -34.06) * mm});
            skLineSegment(sketch, "E788.MirrorCS", {"start": v(25.47, -54.06) * mm, "end": v(24.54, -51.48) * mm});
            skPoint(sketch, "E789.MirrorP", {"position": v(41.35, -33.46) * mm});
            skPoint(sketch, "E790.MirrorP", {"position": v(4.73, -33.46) * mm});
            skPoint(sketch, "E791.MirrorP", {"position": v(32.65, -48) * mm});
            skLineSegment(sketch, "E792.MirrorCS", {"start": v(4.15, -33.61) * mm, "end": v(1.5, -34.32) * mm});
            skPoint(sketch, "E793.MirrorP", {"position": v(9.27, -44.46) * mm});
            skPoint(sketch, "E794.MirrorP", {"position": v(42.04, -43.25) * mm});
            skPoint(sketch, "E795.MirrorP", {"position": v(34.6, -46.69) * mm});
            skPoint(sketch, "E796.MirrorP", {"position": v(41.08, -36.6) * mm});
            skPoint(sketch, "E797.MirrorP", {"position": v(7.6, -42) * mm});
            skPoint(sketch, "E798.MirrorP", {"position": v(6.06, -39.26) * mm});
            skLineSegment(sketch, "E799.MirrorCS", {"start": v(11.06, -46.26) * mm, "end": v(9.7, -44.89) * mm});
            skLineSegment(sketch, "E800.MirrorCS", {"start": v(27.43, -50.97) * mm, "end": v(27.43, -53.71) * mm});
            skPoint(sketch, "E801.MirrorP", {"position": v(25.62, -54.46) * mm});
            skLineSegment(sketch, "E802.MirrorCS", {"start": v(18.66, -54.14) * mm, "end": v(20.47, -54.46) * mm, "construction": true});
            skPoint(sketch, "E803.MirrorP", {"position": v(11.5, -46.69) * mm});
            skPoint(sketch, "E804.MirrorP", {"position": v(36.82, -44.46) * mm});
            skLineSegment(sketch, "E805.MirrorCS", {"start": v(24.93, -50.8) * mm, "end": v(26.84, -50.47) * mm});
            skPoint(sketch, "E806.MirrorP", {"position": v(38.48, -42) * mm});
            skPoint(sketch, "E807.MirrorP", {"position": v(45, -34.43) * mm});
            skPoint(sketch, "E808.MirrorP", {"position": v(5, -36.6) * mm});
            skLineSegment(sketch, "E809.MirrorCS", {"start": v(4.45, -43.11) * mm, "end": v(7.04, -42.2) * mm});
            skPoint(sketch, "E810.MirrorP", {"position": v(29.92, -49.57) * mm});
            skPoint(sketch, "E811.MirrorP", {"position": v(8.4, -48.85) * mm});
            skLineSegment(sketch, "E812.MirrorCS", {"start": v(5.6, -39.64) * mm, "end": v(3.48, -41.38) * mm});
            skLineSegment(sketch, "E813.MirrorCS", {"start": v(7.31, -41.48) * mm, "end": v(6.36, -39.79) * mm});
            skPoint(sketch, "E814.MirrorP", {"position": v(3.15, -41.65) * mm});
            skLineSegment(sketch, "E815.MirrorCS", {"start": v(1.67, -36.3) * mm, "end": v(4.4, -36.54) * mm});
            skSolve(sketch);
        }
        {
            var Q0;
            Q0=makeQuery(id+"F2.imprint","IMPRINT",FACE,{"disambiguationData":[TD([[makeQuery(id+"F2.imprint","IMPRINT",EDGE,{"derivedFrom":sQuery(id+"F2.wireOp",EDGE,"E572")}),1.0]])]});
            extrude(context, id + "F3", {"entities" : qUnion([Q0]), "depth" : 6.35 * mm});
        }
        {
            var Q0;
            Q0=qSketchRegion(id+"F2",true);
            extrude(context, id + "F4", {"entities" : qUnion([Q0]), "operationType" : NewBodyOperationType.ADD, "depth" : 12.7 * mm});
        }
    });
